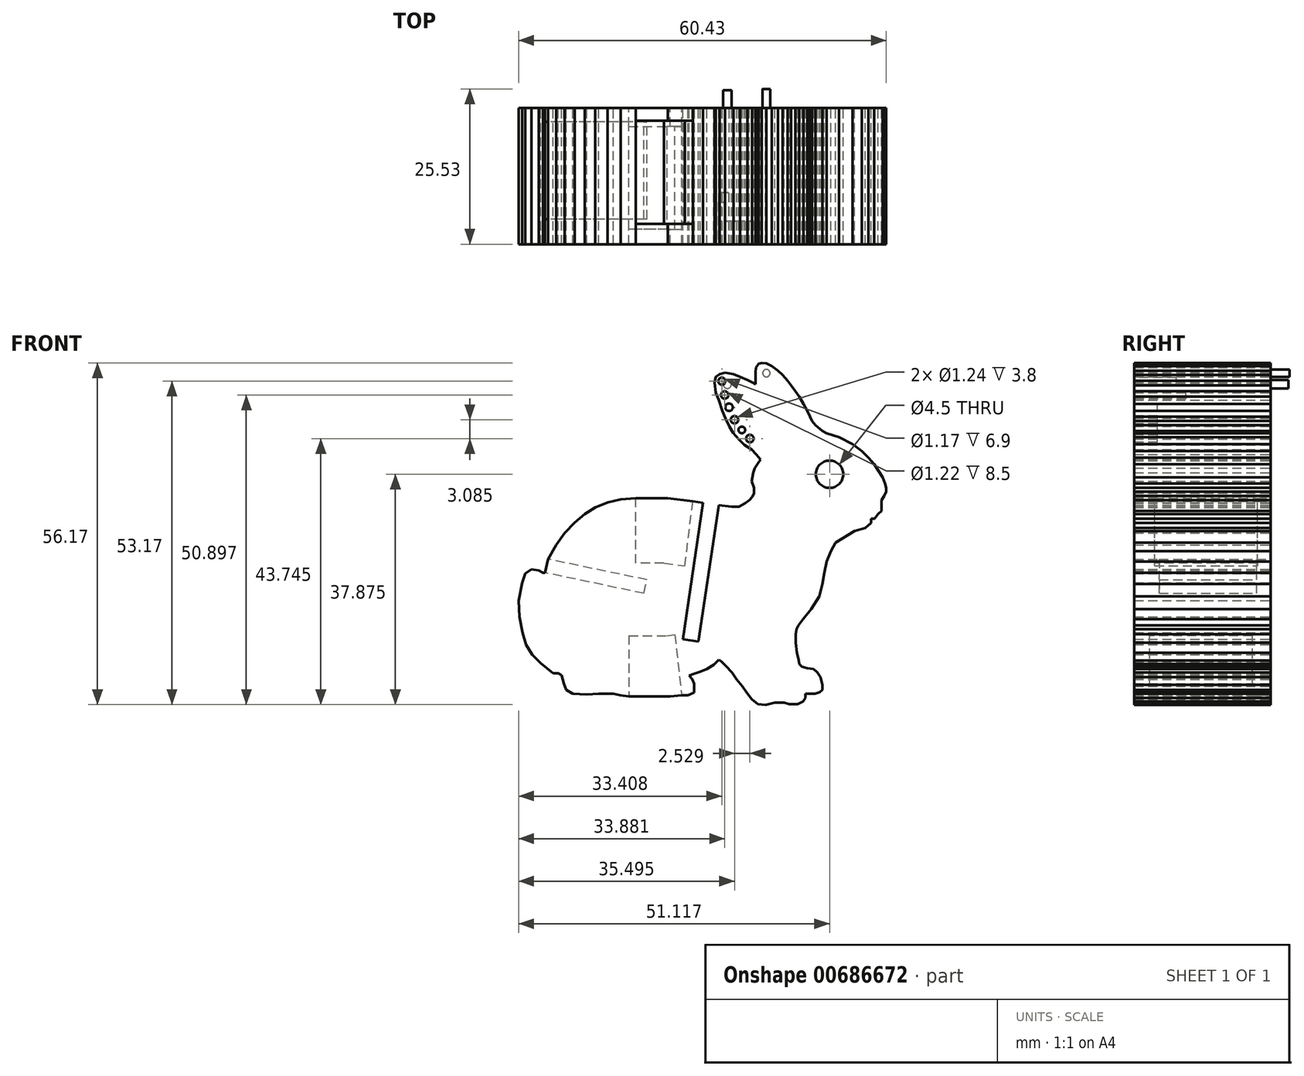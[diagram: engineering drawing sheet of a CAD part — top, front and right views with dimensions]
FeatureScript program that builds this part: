
annotation { "Feature Type Name" : "Feature", "Feature Type Description" : "" }
export const myFeature = defineFeature(function(context is Context, id is Id, definition is map)
    precondition{}
    {
        {
            var Q0;
            Q0=qCreatedBy(makeId("Front.planeOp"),FACE);
            var sketch = newSketch(context, id + "F0", { "sketchPlane" : qUnion([Q0])});
            skLineSegment(sketch, "E0", {"start": v(59.18, 31.9) * mm, "end": v(59.18, 31.2) * mm});
            skLineSegment(sketch, "E1", {"start": v(59.18, 31.2) * mm, "end": v(58.21, 30.37) * mm});
            skLineSegment(sketch, "E2", {"start": v(58.21, 30.37) * mm, "end": v(56.46, 29.85) * mm});
            skLineSegment(sketch, "E3", {"start": v(56.46, 29.85) * mm, "end": v(53.36, 27.96) * mm});
            skLineSegment(sketch, "E4", {"start": v(53.36, 27.96) * mm, "end": v(52.57, 26.52) * mm});
            skLineSegment(sketch, "E5", {"start": v(52.57, 26.52) * mm, "end": v(51.91, 24.8) * mm});
            skLineSegment(sketch, "E6", {"start": v(51.91, 24.8) * mm, "end": v(51.53, 22.99) * mm});
            skLineSegment(sketch, "E7", {"start": v(51.53, 22.99) * mm, "end": v(51.19, 21.11) * mm});
            skLineSegment(sketch, "E8", {"start": v(51.19, 21.11) * mm, "end": v(50.68, 19.1) * mm});
            skLineSegment(sketch, "E9", {"start": v(50.68, 19.1) * mm, "end": v(49.32, 17.01) * mm});
            skLineSegment(sketch, "E10", {"start": v(49.32, 17.01) * mm, "end": v(48.02, 15.39) * mm});
            skLineSegment(sketch, "E11", {"start": v(48.02, 15.39) * mm, "end": v(47.24, 14.33) * mm});
            skLineSegment(sketch, "E12", {"start": v(47.24, 14.33) * mm, "end": v(46.93, 13.71) * mm});
            skLineSegment(sketch, "E13", {"start": v(46.93, 13.71) * mm, "end": v(46.8, 12.88) * mm});
            skLineSegment(sketch, "E14", {"start": v(46.8, 12.88) * mm, "end": v(46.8, 11.49) * mm});
            skLineSegment(sketch, "E15", {"start": v(46.8, 11.49) * mm, "end": v(47.02, 9.82) * mm});
            skLineSegment(sketch, "E16", {"start": v(47.02, 9.82) * mm, "end": v(47.3, 8.54) * mm});
            skLineSegment(sketch, "E17", {"start": v(47.3, 8.54) * mm, "end": v(47.4, 8) * mm});
            skLineSegment(sketch, "E18", {"start": v(47.4, 8) * mm, "end": v(47.8, 7.53) * mm});
            skLineSegment(sketch, "E19", {"start": v(47.8, 7.53) * mm, "end": v(48.73, 7.33) * mm});
            skLineSegment(sketch, "E20", {"start": v(48.73, 7.33) * mm, "end": v(49.72, 7.17) * mm});
            skLineSegment(sketch, "E21", {"start": v(49.72, 7.17) * mm, "end": v(50.33, 6.61) * mm});
            skLineSegment(sketch, "E22", {"start": v(50.33, 6.61) * mm, "end": v(50.85, 5.82) * mm});
            skLineSegment(sketch, "E23", {"start": v(50.85, 5.82) * mm, "end": v(51.16, 4.55) * mm});
            skLineSegment(sketch, "E24", {"start": v(51.16, 4.55) * mm, "end": v(51.16, 3.77) * mm});
            skLineSegment(sketch, "E25", {"start": v(51.16, 3.77) * mm, "end": v(50.77, 3.37) * mm});
            skLineSegment(sketch, "E26", {"start": v(50.77, 3.37) * mm, "end": v(49.97, 3.1) * mm});
            skLineSegment(sketch, "E27", {"start": v(49.97, 3.1) * mm, "end": v(48.4, 3.1) * mm});
            skLineSegment(sketch, "E28", {"start": v(48.4, 3.1) * mm, "end": v(48.4, 2.43) * mm});
            skLineSegment(sketch, "E29", {"start": v(48.4, 2.43) * mm, "end": v(48.04, 1.82) * mm});
            skLineSegment(sketch, "E30", {"start": v(48.04, 1.82) * mm, "end": v(47.14, 1.41) * mm});
            skLineSegment(sketch, "E31", {"start": v(47.14, 1.41) * mm, "end": v(45.74, 1.41) * mm});
            skLineSegment(sketch, "E32", {"start": v(45.74, 1.41) * mm, "end": v(44.91, 1.62) * mm});
            skLineSegment(sketch, "E33", {"start": v(44.91, 1.62) * mm, "end": v(43.35, 1.62) * mm});
            skLineSegment(sketch, "E34", {"start": v(43.35, 1.62) * mm, "end": v(41.85, 1.3) * mm});
            skLineSegment(sketch, "E35", {"start": v(41.85, 1.3) * mm, "end": v(40.56, 1.41) * mm});
            skLineSegment(sketch, "E36", {"start": v(40.56, 1.41) * mm, "end": v(39.54, 2.2) * mm});
            skLineSegment(sketch, "E37", {"start": v(39.54, 2.2) * mm, "end": v(38.77, 3.29) * mm});
            skLineSegment(sketch, "E38", {"start": v(38.77, 3.29) * mm, "end": v(38.07, 4.3) * mm});
            skLineSegment(sketch, "E39", {"start": v(38.07, 4.3) * mm, "end": v(37.07, 5.46) * mm});
            skLineSegment(sketch, "E40", {"start": v(37.07, 5.46) * mm, "end": v(36.3, 6.57) * mm});
            skLineSegment(sketch, "E41", {"start": v(36.3, 6.57) * mm, "end": v(35.28, 7.7) * mm});
            skLineSegment(sketch, "E42", {"start": v(35.28, 7.7) * mm, "end": v(34.6, 8.39) * mm});
            skLineSegment(sketch, "E43", {"start": v(34.6, 8.39) * mm, "end": v(34.18, 8.68) * mm});
            skLineSegment(sketch, "E44", {"start": v(34.18, 8.68) * mm, "end": v(33.34, 7.84) * mm});
            skLineSegment(sketch, "E45", {"start": v(33.34, 7.84) * mm, "end": v(32.19, 7.18) * mm});
            skLineSegment(sketch, "E46", {"start": v(32.19, 7.18) * mm, "end": v(31.1, 6.72) * mm});
            skLineSegment(sketch, "E47", {"start": v(31.1, 6.72) * mm, "end": v(30.18, 6.39) * mm});
            skLineSegment(sketch, "E48", {"start": v(30.18, 6.39) * mm, "end": v(29.26, 6.12) * mm});
            skLineSegment(sketch, "E49", {"start": v(29.26, 6.12) * mm, "end": v(29.8, 5.51) * mm});
            skLineSegment(sketch, "E50", {"start": v(29.8, 5.51) * mm, "end": v(30.13, 4.73) * mm});
            skLineSegment(sketch, "E51", {"start": v(30.13, 4.73) * mm, "end": v(30.13, 4.07) * mm});
            skLineSegment(sketch, "E52", {"start": v(30.13, 4.07) * mm, "end": v(30.13, 3.51) * mm});
            skLineSegment(sketch, "E53", {"start": v(30.13, 3.51) * mm, "end": v(30.13, 3.29) * mm});
            skLineSegment(sketch, "E54", {"start": v(30.13, 3.29) * mm, "end": v(29.07, 2.88) * mm});
            skLineSegment(sketch, "E55", {"start": v(29.07, 2.88) * mm, "end": v(28.07, 2.88) * mm});
            skLineSegment(sketch, "E56", {"start": v(28.07, 2.88) * mm, "end": v(26.19, 2.66) * mm});
            skLineSegment(sketch, "E57", {"start": v(26.19, 2.66) * mm, "end": v(23.74, 2.66) * mm});
            skLineSegment(sketch, "E58", {"start": v(23.74, 2.66) * mm, "end": v(21.88, 2.66) * mm});
            skLineSegment(sketch, "E59", {"start": v(21.88, 2.66) * mm, "end": v(19.4, 2.66) * mm});
            skLineSegment(sketch, "E60", {"start": v(19.4, 2.66) * mm, "end": v(18, 2.88) * mm});
            skLineSegment(sketch, "E61", {"start": v(18, 2.88) * mm, "end": v(16.82, 3.14) * mm});
            skLineSegment(sketch, "E62", {"start": v(16.82, 3.14) * mm, "end": v(14.45, 3.14) * mm});
            skLineSegment(sketch, "E63", {"start": v(14.45, 3.14) * mm, "end": v(12.45, 3) * mm});
            skLineSegment(sketch, "E64", {"start": v(12.45, 3) * mm, "end": v(10.14, 3.13) * mm});
            skLineSegment(sketch, "E65", {"start": v(10.14, 3.13) * mm, "end": v(9.06, 3.73) * mm});
            skLineSegment(sketch, "E66", {"start": v(9.06, 3.73) * mm, "end": v(8.7, 4.73) * mm});
            skLineSegment(sketch, "E67", {"start": v(8.7, 4.73) * mm, "end": v(8.3, 6.14) * mm});
            skLineSegment(sketch, "E68", {"start": v(8.3, 6.14) * mm, "end": v(7.74, 6.47) * mm});
            skLineSegment(sketch, "E69", {"start": v(7.74, 6.47) * mm, "end": v(6.93, 6.47) * mm});
            skLineSegment(sketch, "E70", {"start": v(6.93, 6.47) * mm, "end": v(4.9, 8.14) * mm});
            skLineSegment(sketch, "E71", {"start": v(4.9, 8.14) * mm, "end": v(3.53, 9.54) * mm});
            skLineSegment(sketch, "E72", {"start": v(3.53, 9.54) * mm, "end": v(2.47, 11.15) * mm});
            skLineSegment(sketch, "E73", {"start": v(2.47, 11.15) * mm, "end": v(1.9, 13.14) * mm});
            skLineSegment(sketch, "E74", {"start": v(1.9, 13.14) * mm, "end": v(1.4, 15.75) * mm});
            skLineSegment(sketch, "E75", {"start": v(1.4, 15.75) * mm, "end": v(1.25, 18.43) * mm});
            skLineSegment(sketch, "E76", {"start": v(1.25, 18.43) * mm, "end": v(1.86, 21.3) * mm});
            skLineSegment(sketch, "E77", {"start": v(1.86, 21.3) * mm, "end": v(2.39, 22.87) * mm});
            skLineSegment(sketch, "E78", {"start": v(2.39, 22.87) * mm, "end": v(3.37, 23.56) * mm});
            skLineSegment(sketch, "E79", {"start": v(3.37, 23.56) * mm, "end": v(4.55, 23.4) * mm});
            skLineSegment(sketch, "E80", {"start": v(4.55, 23.4) * mm, "end": v(5.28, 22.99) * mm});
            skLineSegment(sketch, "E81", {"start": v(5.28, 22.99) * mm, "end": v(5.63, 22.99) * mm});
            skLineSegment(sketch, "E82", {"start": v(5.63, 22.99) * mm, "end": v(6.1, 25.22) * mm});
            skLineSegment(sketch, "E83", {"start": v(6.1, 25.22) * mm, "end": v(7.44, 27.53) * mm});
            skLineSegment(sketch, "E84", {"start": v(7.44, 27.53) * mm, "end": v(8.84, 29.53) * mm});
            skLineSegment(sketch, "E85", {"start": v(8.84, 29.53) * mm, "end": v(10.46, 31.27) * mm});
            skLineSegment(sketch, "E86", {"start": v(10.46, 31.27) * mm, "end": v(12.13, 32.66) * mm});
            skLineSegment(sketch, "E87", {"start": v(12.13, 32.66) * mm, "end": v(13.85, 33.74) * mm});
            skLineSegment(sketch, "E88", {"start": v(13.85, 33.74) * mm, "end": v(15.89, 34.56) * mm});
            skLineSegment(sketch, "E89", {"start": v(15.89, 34.56) * mm, "end": v(18.07, 35.02) * mm});
            skLineSegment(sketch, "E90", {"start": v(18.07, 35.02) * mm, "end": v(20.5, 35.25) * mm});
            skLineSegment(sketch, "E91", {"start": v(20.5, 35.25) * mm, "end": v(22.93, 35.25) * mm});
            skLineSegment(sketch, "E92", {"start": v(22.93, 35.25) * mm, "end": v(25.8, 35.25) * mm});
            skLineSegment(sketch, "E93", {"start": v(25.8, 35.25) * mm, "end": v(29.9, 34.74) * mm});
            skLineSegment(sketch, "E94", {"start": v(29.9, 34.74) * mm, "end": v(31.58, 34.5) * mm});
            skLineSegment(sketch, "E95", {"start": v(31.58, 34.5) * mm, "end": v(34.17, 34.11) * mm});
            skLineSegment(sketch, "E96", {"start": v(34.17, 34.11) * mm, "end": v(36.24, 33.84) * mm});
            skLineSegment(sketch, "E97", {"start": v(36.24, 33.84) * mm, "end": v(37.5, 33.84) * mm});
            skLineSegment(sketch, "E98", {"start": v(37.5, 33.84) * mm, "end": v(38.48, 34.41) * mm});
            skLineSegment(sketch, "E99", {"start": v(38.48, 34.41) * mm, "end": v(39.21, 34.95) * mm});
            skLineSegment(sketch, "E100", {"start": v(39.21, 34.95) * mm, "end": v(39.69, 35.51) * mm});
            skLineSegment(sketch, "E101", {"start": v(39.69, 35.51) * mm, "end": v(39.94, 36.1) * mm});
            skLineSegment(sketch, "E102", {"start": v(39.94, 36.1) * mm, "end": v(39.94, 36.93) * mm});
            skLineSegment(sketch, "E103", {"start": v(39.94, 36.93) * mm, "end": v(39.54, 38.02) * mm});
            skLineSegment(sketch, "E104", {"start": v(39.54, 38.02) * mm, "end": v(39.83, 39.44) * mm});
            skLineSegment(sketch, "E105", {"start": v(39.83, 39.44) * mm, "end": v(40.08, 40.2) * mm});
            skLineSegment(sketch, "E106", {"start": v(40.08, 40.2) * mm, "end": v(40.6, 40.94) * mm});
            skLineSegment(sketch, "E107", {"start": v(40.6, 40.94) * mm, "end": v(41, 41.61) * mm});
            skLineSegment(sketch, "E108", {"start": v(41, 41.61) * mm, "end": v(40.3, 42.4) * mm});
            skLineSegment(sketch, "E109", {"start": v(40.3, 42.4) * mm, "end": v(39.57, 43.22) * mm});
            skLineSegment(sketch, "E110", {"start": v(39.57, 43.22) * mm, "end": v(38.4, 44.03) * mm});
            skLineSegment(sketch, "E111", {"start": v(38.4, 44.03) * mm, "end": v(37.38, 44.92) * mm});
            skLineSegment(sketch, "E112", {"start": v(37.38, 44.92) * mm, "end": v(36.53, 45.97) * mm});
            skLineSegment(sketch, "E113", {"start": v(36.53, 45.97) * mm, "end": v(35.9, 47.05) * mm});
            skLineSegment(sketch, "E114", {"start": v(35.9, 47.05) * mm, "end": v(35.26, 48.39) * mm});
            skLineSegment(sketch, "E115", {"start": v(35.26, 48.39) * mm, "end": v(34.77, 49.59) * mm});
            skLineSegment(sketch, "E116", {"start": v(34.77, 49.59) * mm, "end": v(34.17, 51.34) * mm});
            skLineSegment(sketch, "E117", {"start": v(34.17, 51.34) * mm, "end": v(33.68, 52.6) * mm});
            skLineSegment(sketch, "E118", {"start": v(33.68, 52.6) * mm, "end": v(33.5, 54.23) * mm});
            skLineSegment(sketch, "E119", {"start": v(33.5, 54.23) * mm, "end": v(33.67, 55.17) * mm});
            skLineSegment(sketch, "E120", {"start": v(33.67, 55.17) * mm, "end": v(34.28, 55.63) * mm});
            skLineSegment(sketch, "E121", {"start": v(34.28, 55.63) * mm, "end": v(35.19, 55.89) * mm});
            skLineSegment(sketch, "E122", {"start": v(35.19, 55.89) * mm, "end": v(36.57, 55.6) * mm});
            skLineSegment(sketch, "E123", {"start": v(36.57, 55.6) * mm, "end": v(37.7, 55.18) * mm});
            skLineSegment(sketch, "E124", {"start": v(37.7, 55.18) * mm, "end": v(38.87, 54.67) * mm});
            skLineSegment(sketch, "E125", {"start": v(38.87, 54.67) * mm, "end": v(39.6, 54.27) * mm});
            skLineSegment(sketch, "E126", {"start": v(39.6, 54.27) * mm, "end": v(40.2, 53.98) * mm});
            skLineSegment(sketch, "E127", {"start": v(40.2, 53.98) * mm, "end": v(40.2, 55.95) * mm});
            skLineSegment(sketch, "E128", {"start": v(40.2, 55.95) * mm, "end": v(40.3, 56.68) * mm});
            skLineSegment(sketch, "E129", {"start": v(40.3, 56.68) * mm, "end": v(40.7, 57.32) * mm});
            skLineSegment(sketch, "E130", {"start": v(40.7, 57.32) * mm, "end": v(41.2, 57.47) * mm});
            skLineSegment(sketch, "E131", {"start": v(41.2, 57.47) * mm, "end": v(41.98, 57.38) * mm});
            skLineSegment(sketch, "E132", {"start": v(41.98, 57.38) * mm, "end": v(42.9, 56.96) * mm});
            skLineSegment(sketch, "E133", {"start": v(42.9, 56.96) * mm, "end": v(43.88, 56.18) * mm});
            skLineSegment(sketch, "E134", {"start": v(43.88, 56.18) * mm, "end": v(44.66, 55.47) * mm});
            skLineSegment(sketch, "E135", {"start": v(44.66, 55.47) * mm, "end": v(45.46, 54.57) * mm});
            skLineSegment(sketch, "E136", {"start": v(45.46, 54.57) * mm, "end": v(46.07, 53.8) * mm});
            skLineSegment(sketch, "E137", {"start": v(46.07, 53.8) * mm, "end": v(46.74, 52.83) * mm});
            skLineSegment(sketch, "E138", {"start": v(46.74, 52.83) * mm, "end": v(47.4, 51.92) * mm});
            skLineSegment(sketch, "E139", {"start": v(47.4, 51.92) * mm, "end": v(48.07, 50.76) * mm});
            skLineSegment(sketch, "E140", {"start": v(48.07, 50.76) * mm, "end": v(48.69, 49.58) * mm});
            skLineSegment(sketch, "E141", {"start": v(48.69, 49.58) * mm, "end": v(49.16, 48.64) * mm});
            skLineSegment(sketch, "E142", {"start": v(49.16, 48.64) * mm, "end": v(49.5, 47.92) * mm});
            skLineSegment(sketch, "E143", {"start": v(49.5, 47.92) * mm, "end": v(50.03, 47.25) * mm});
            skLineSegment(sketch, "E144", {"start": v(50.03, 47.25) * mm, "end": v(51.16, 46.28) * mm});
            skLineSegment(sketch, "E145", {"start": v(51.16, 46.28) * mm, "end": v(51.87, 45.89) * mm});
            skLineSegment(sketch, "E146", {"start": v(51.87, 45.89) * mm, "end": v(53.94, 45.3) * mm});
            skLineSegment(sketch, "E147", {"start": v(53.94, 45.3) * mm, "end": v(56.13, 44.1) * mm});
            skLineSegment(sketch, "E148", {"start": v(56.13, 44.1) * mm, "end": v(57.69, 42.96) * mm});
            skLineSegment(sketch, "E149", {"start": v(57.69, 42.96) * mm, "end": v(58.76, 41.92) * mm});
            skLineSegment(sketch, "E150", {"start": v(58.76, 41.92) * mm, "end": v(59.7, 40.84) * mm});
            skLineSegment(sketch, "E151", {"start": v(59.7, 40.84) * mm, "end": v(60.39, 39.73) * mm});
            skLineSegment(sketch, "E152", {"start": v(60.39, 39.73) * mm, "end": v(61.06, 38.64) * mm});
            skLineSegment(sketch, "E153", {"start": v(61.06, 38.64) * mm, "end": v(61.48, 37.65) * mm});
            skLineSegment(sketch, "E154", {"start": v(61.48, 37.65) * mm, "end": v(61.68, 36.96) * mm});
            skLineSegment(sketch, "E155", {"start": v(61.68, 36.96) * mm, "end": v(61.68, 36.3) * mm});
            skLineSegment(sketch, "E156", {"start": v(61.68, 36.3) * mm, "end": v(61.36, 35.64) * mm});
            skLineSegment(sketch, "E157", {"start": v(61.36, 35.64) * mm, "end": v(60.9, 34.95) * mm});
            skLineSegment(sketch, "E158", {"start": v(60.9, 34.95) * mm, "end": v(60.9, 33.94) * mm});
            skLineSegment(sketch, "E159", {"start": v(60.9, 33.94) * mm, "end": v(60.9, 33.16) * mm});
            skLineSegment(sketch, "E160", {"start": v(60.9, 33.16) * mm, "end": v(60.3, 32.6) * mm});
            skLineSegment(sketch, "E161", {"start": v(60.3, 32.6) * mm, "end": v(59.74, 31.88) * mm});
            skLineSegment(sketch, "E162", {"start": v(59.74, 31.88) * mm, "end": v(59.18, 31.9) * mm});
            skCircle(sketch, "E163", {"center": v(52.37, 39.17) * mm, "radius": 2.25 * mm});
            skSolve(sketch);
        }
        {
            var Q0;
            Q0=makeQuery(id+"F0.imprint","IMPRINT",FACE,{"disambiguationData":[TD([[makeQuery(id+"F0.imprint","IMPRINT",EDGE,{"derivedFrom":sQuery(id+"F0.wireOp",EDGE,"E0")}),-1.0]])]});
            extrude(context, id + "F1", {"entities" : qUnion([Q0]), "depth" : 3 * mm, "offsetDistance" : 25 * mm});
        }
        {
            var Q0;
            Q0=makeQuery(id+"F1.opExtrude","CAP_FACE",FACE,{"disambiguationData":[OSD([sQuery(id+"F0.wireOp",EDGE,"E0"),sQuery(id+"F0.wireOp",EDGE,"E1"),sQuery(id+"F0.wireOp",EDGE,"E2"),sQuery(id+"F0.wireOp",EDGE,"E3"),sQuery(id+"F0.wireOp",EDGE,"E4"),sQuery(id+"F0.wireOp",EDGE,"E5"),sQuery(id+"F0.wireOp",EDGE,"E6"),sQuery(id+"F0.wireOp",EDGE,"E7"),sQuery(id+"F0.wireOp",EDGE,"E8"),sQuery(id+"F0.wireOp",EDGE,"E9"),sQuery(id+"F0.wireOp",EDGE,"E10"),sQuery(id+"F0.wireOp",EDGE,"E11"),sQuery(id+"F0.wireOp",EDGE,"E12"),sQuery(id+"F0.wireOp",EDGE,"E13"),sQuery(id+"F0.wireOp",EDGE,"E14"),sQuery(id+"F0.wireOp",EDGE,"E15"),sQuery(id+"F0.wireOp",EDGE,"E16"),sQuery(id+"F0.wireOp",EDGE,"E17"),sQuery(id+"F0.wireOp",EDGE,"E18"),sQuery(id+"F0.wireOp",EDGE,"E19"),sQuery(id+"F0.wireOp",EDGE,"E20"),sQuery(id+"F0.wireOp",EDGE,"E21"),sQuery(id+"F0.wireOp",EDGE,"E22"),sQuery(id+"F0.wireOp",EDGE,"E23"),sQuery(id+"F0.wireOp",EDGE,"E24"),sQuery(id+"F0.wireOp",EDGE,"E25"),sQuery(id+"F0.wireOp",EDGE,"E26"),sQuery(id+"F0.wireOp",EDGE,"E27"),sQuery(id+"F0.wireOp",EDGE,"E28"),sQuery(id+"F0.wireOp",EDGE,"E29"),sQuery(id+"F0.wireOp",EDGE,"E30"),sQuery(id+"F0.wireOp",EDGE,"E31"),sQuery(id+"F0.wireOp",EDGE,"E32"),sQuery(id+"F0.wireOp",EDGE,"E33"),sQuery(id+"F0.wireOp",EDGE,"E34"),sQuery(id+"F0.wireOp",EDGE,"E35"),sQuery(id+"F0.wireOp",EDGE,"E36"),sQuery(id+"F0.wireOp",EDGE,"E37"),sQuery(id+"F0.wireOp",EDGE,"E38"),sQuery(id+"F0.wireOp",EDGE,"E39"),sQuery(id+"F0.wireOp",EDGE,"E40"),sQuery(id+"F0.wireOp",EDGE,"E41"),sQuery(id+"F0.wireOp",EDGE,"E42"),sQuery(id+"F0.wireOp",EDGE,"E43"),sQuery(id+"F0.wireOp",EDGE,"E44"),sQuery(id+"F0.wireOp",EDGE,"E45"),sQuery(id+"F0.wireOp",EDGE,"E46"),sQuery(id+"F0.wireOp",EDGE,"E47"),sQuery(id+"F0.wireOp",EDGE,"E48"),sQuery(id+"F0.wireOp",EDGE,"E49"),sQuery(id+"F0.wireOp",EDGE,"E50"),sQuery(id+"F0.wireOp",EDGE,"E51"),sQuery(id+"F0.wireOp",EDGE,"E52"),sQuery(id+"F0.wireOp",EDGE,"E53"),sQuery(id+"F0.wireOp",EDGE,"E54"),sQuery(id+"F0.wireOp",EDGE,"E55"),sQuery(id+"F0.wireOp",EDGE,"E56"),sQuery(id+"F0.wireOp",EDGE,"E57"),sQuery(id+"F0.wireOp",EDGE,"E58"),sQuery(id+"F0.wireOp",EDGE,"E59"),sQuery(id+"F0.wireOp",EDGE,"E60"),sQuery(id+"F0.wireOp",EDGE,"E61"),sQuery(id+"F0.wireOp",EDGE,"E62"),sQuery(id+"F0.wireOp",EDGE,"E63"),sQuery(id+"F0.wireOp",EDGE,"E64"),sQuery(id+"F0.wireOp",EDGE,"E65"),sQuery(id+"F0.wireOp",EDGE,"E66"),sQuery(id+"F0.wireOp",EDGE,"E67"),sQuery(id+"F0.wireOp",EDGE,"E68"),sQuery(id+"F0.wireOp",EDGE,"E69"),sQuery(id+"F0.wireOp",EDGE,"E70"),sQuery(id+"F0.wireOp",EDGE,"E71"),sQuery(id+"F0.wireOp",EDGE,"E72"),sQuery(id+"F0.wireOp",EDGE,"E73"),sQuery(id+"F0.wireOp",EDGE,"E74"),sQuery(id+"F0.wireOp",EDGE,"E75"),sQuery(id+"F0.wireOp",EDGE,"E76"),sQuery(id+"F0.wireOp",EDGE,"E77"),sQuery(id+"F0.wireOp",EDGE,"E78"),sQuery(id+"F0.wireOp",EDGE,"E79"),sQuery(id+"F0.wireOp",EDGE,"E80"),sQuery(id+"F0.wireOp",EDGE,"E81"),sQuery(id+"F0.wireOp",EDGE,"E82"),sQuery(id+"F0.wireOp",EDGE,"E83"),sQuery(id+"F0.wireOp",EDGE,"E84"),sQuery(id+"F0.wireOp",EDGE,"E85"),sQuery(id+"F0.wireOp",EDGE,"E86"),sQuery(id+"F0.wireOp",EDGE,"E87"),sQuery(id+"F0.wireOp",EDGE,"E88"),sQuery(id+"F0.wireOp",EDGE,"E89"),sQuery(id+"F0.wireOp",EDGE,"E90"),sQuery(id+"F0.wireOp",EDGE,"E91"),sQuery(id+"F0.wireOp",EDGE,"E92"),sQuery(id+"F0.wireOp",EDGE,"E93"),sQuery(id+"F0.wireOp",EDGE,"E94"),sQuery(id+"F0.wireOp",EDGE,"E95"),sQuery(id+"F0.wireOp",EDGE,"E96"),sQuery(id+"F0.wireOp",EDGE,"E97"),sQuery(id+"F0.wireOp",EDGE,"E98"),sQuery(id+"F0.wireOp",EDGE,"E99"),sQuery(id+"F0.wireOp",EDGE,"E100"),sQuery(id+"F0.wireOp",EDGE,"E101"),sQuery(id+"F0.wireOp",EDGE,"E102"),sQuery(id+"F0.wireOp",EDGE,"E103"),sQuery(id+"F0.wireOp",EDGE,"E104"),sQuery(id+"F0.wireOp",EDGE,"E105"),sQuery(id+"F0.wireOp",EDGE,"E106"),sQuery(id+"F0.wireOp",EDGE,"E107"),sQuery(id+"F0.wireOp",EDGE,"E108"),sQuery(id+"F0.wireOp",EDGE,"E109"),sQuery(id+"F0.wireOp",EDGE,"E110"),sQuery(id+"F0.wireOp",EDGE,"E111"),sQuery(id+"F0.wireOp",EDGE,"E112"),sQuery(id+"F0.wireOp",EDGE,"E113"),sQuery(id+"F0.wireOp",EDGE,"E114"),sQuery(id+"F0.wireOp",EDGE,"E115"),sQuery(id+"F0.wireOp",EDGE,"E116"),sQuery(id+"F0.wireOp",EDGE,"E117"),sQuery(id+"F0.wireOp",EDGE,"E118"),sQuery(id+"F0.wireOp",EDGE,"E119"),sQuery(id+"F0.wireOp",EDGE,"E120"),sQuery(id+"F0.wireOp",EDGE,"E121"),sQuery(id+"F0.wireOp",EDGE,"E122"),sQuery(id+"F0.wireOp",EDGE,"E123"),sQuery(id+"F0.wireOp",EDGE,"E124"),sQuery(id+"F0.wireOp",EDGE,"E125"),sQuery(id+"F0.wireOp",EDGE,"E126"),sQuery(id+"F0.wireOp",EDGE,"E127"),sQuery(id+"F0.wireOp",EDGE,"E128"),sQuery(id+"F0.wireOp",EDGE,"E129"),sQuery(id+"F0.wireOp",EDGE,"E130"),sQuery(id+"F0.wireOp",EDGE,"E131"),sQuery(id+"F0.wireOp",EDGE,"E132"),sQuery(id+"F0.wireOp",EDGE,"E133"),sQuery(id+"F0.wireOp",EDGE,"E134"),sQuery(id+"F0.wireOp",EDGE,"E135"),sQuery(id+"F0.wireOp",EDGE,"E136"),sQuery(id+"F0.wireOp",EDGE,"E137"),sQuery(id+"F0.wireOp",EDGE,"E138"),sQuery(id+"F0.wireOp",EDGE,"E139"),sQuery(id+"F0.wireOp",EDGE,"E140"),sQuery(id+"F0.wireOp",EDGE,"E141"),sQuery(id+"F0.wireOp",EDGE,"E142"),sQuery(id+"F0.wireOp",EDGE,"E143"),sQuery(id+"F0.wireOp",EDGE,"E144"),sQuery(id+"F0.wireOp",EDGE,"E145"),sQuery(id+"F0.wireOp",EDGE,"E146"),sQuery(id+"F0.wireOp",EDGE,"E147"),sQuery(id+"F0.wireOp",EDGE,"E148"),sQuery(id+"F0.wireOp",EDGE,"E149"),sQuery(id+"F0.wireOp",EDGE,"E150"),sQuery(id+"F0.wireOp",EDGE,"E151"),sQuery(id+"F0.wireOp",EDGE,"E152"),sQuery(id+"F0.wireOp",EDGE,"E153"),sQuery(id+"F0.wireOp",EDGE,"E154"),sQuery(id+"F0.wireOp",EDGE,"E155"),sQuery(id+"F0.wireOp",EDGE,"E156"),sQuery(id+"F0.wireOp",EDGE,"E157"),sQuery(id+"F0.wireOp",EDGE,"E158"),sQuery(id+"F0.wireOp",EDGE,"E159"),sQuery(id+"F0.wireOp",EDGE,"E160"),sQuery(id+"F0.wireOp",EDGE,"E161"),sQuery(id+"F0.wireOp",EDGE,"E162"),sQuery(id+"F0.wireOp",EDGE,"E163")])],"isStart":false});
            extrude(context, id + "F2", {"entities" : qUnion([Q0]), "operationType" : NewBodyOperationType.ADD, "depth" : 19.4 * mm, "offsetDistance" : 25 * mm});
        }
        {
            var Q0;
            {var subQ0=sQuery(id+"F0.wireOp",EDGE,"E95");Q0=makeQuery(id+"F2.boolean.opBoolean","MERGE",FACE,{"derivedFrom":[makeQuery(id+"F1.opExtrude","SWEPT_FACE",FACE,{"disambiguationData":[OSD([subQ0])]}),makeQuery(id+"F2.opExtrude","SWEPT_FACE",FACE,{"disambiguationData":[OSD([subQ0])]})]});}
            extrude(context, id + "F3", {"entities" : qUnion([Q0]), "operationType" : NewBodyOperationType.REMOVE, "oppositeDirection" : true, "depth" : 15.7 * mm, "offsetDistance" : 25 * mm});
        }
        {
            var Q0;
            Q0=makeQuery(id+"F3.boolean.opBoolean","COPY",FACE,{"derivedFrom":makeQuery(id+"F3.opExtrude","CAP_FACE",FACE,{"disambiguationData":[OSD([sQuery(id+"F0.wireOp",EDGE,"E95")])],"isStart":false})});
            extrude(context, id + "F4", {"entities" : qUnion([Q0]), "operationType" : NewBodyOperationType.REMOVE, "oppositeDirection" : true, "depth" : 7 * mm, "offsetDistance" : 25 * mm});
        }
        {
            var Q0;
            {var subQ0=sQuery(id+"F0.wireOp",EDGE,"E93");Q0=makeQuery(id+"F2.boolean.opBoolean","MERGE",FACE,{"derivedFrom":[makeQuery(id+"F1.opExtrude","SWEPT_FACE",FACE,{"disambiguationData":[OSD([subQ0])]}),makeQuery(id+"F2.opExtrude","SWEPT_FACE",FACE,{"disambiguationData":[OSD([subQ0])]})]});}
            var sketch = newSketch(context, id + "F5", { "sketchPlane" : qUnion([Q0])});
            skLineSegment(sketch, "E164", {"start": v(21.27, -2.12) * mm, "end": v(25.4, -2.12) * mm});
            skLineSegment(sketch, "E165", {"start": v(25.4, -2.12) * mm, "end": v(25.4, -19.03) * mm});
            skLineSegment(sketch, "E166", {"start": v(25.4, -19.03) * mm, "end": v(21.27, -19.03) * mm});
            skLineSegment(sketch, "E167", {"start": v(21.27, -19.03) * mm, "end": v(21.27, -2.12) * mm});
            skSolve(sketch);
        }
        {
            var Q0;
            Q0 = qSketchRegion(id + "F5", true);
            extrude(context, id + "F6", {"entities" : qUnion([Q0]), "operationType" : NewBodyOperationType.REMOVE, "oppositeDirection" : true, "depth" : 10.7 * mm, "offsetDistance" : 25 * mm});
        }
        {
            var Q0;
            {var subQ0=sQuery(id+"F0.wireOp",EDGE,"E92");var subQ1=sQuery(id+"F0.wireOp",EDGE,"E91");Q0=makeQuery(id+"F2.boolean.opBoolean","MERGE",FACE,{"derivedFrom":[makeQuery(id+"F1.opExtrude","SWEPT_FACE",FACE,{"disambiguationData":[OSD([subQ1,subQ0])]}),makeQuery(id+"F2.opExtrude","SWEPT_FACE",FACE,{"disambiguationData":[OSD([subQ1,subQ0])]})]});}
            var sketch = newSketch(context, id + "F7", { "sketchPlane" : qUnion([Q0])});
            skLineSegment(sketch, "E168", {"start": v(25.8, -2.12) * mm, "end": v(20.5, -2.12) * mm});
            skLineSegment(sketch, "E169", {"start": v(20.5, -2.12) * mm, "end": v(20.5, -19.03) * mm});
            skLineSegment(sketch, "E170", {"start": v(20.5, -19.03) * mm, "end": v(25.8, -19.03) * mm});
            skSolve(sketch);
        }
        {
            var Q0;
            Q0 = qSketchRegion(id + "F7", true);
            var Q1;
            Q1=makeQuery(id+"F7.imprint","IMPRINT",FACE,{"disambiguationData":[TD([[makeQuery(id+"F7.imprint","IMPRINT",EDGE,{"derivedFrom":sQuery(id+"F7.wireOp",EDGE,"E168")}),1.0]])]});
            extrude(context, id + "F8", {"entities" : qUnion([Q0, Q1]), "operationType" : NewBodyOperationType.REMOVE, "oppositeDirection" : true, "depth" : 10.7 * mm, "offsetDistance" : 25 * mm});
        }
        {
            var Q0;
            {var subQ0=sQuery(id+"F0.wireOp",EDGE,"E82");Q0=makeQuery(id+"F2.boolean.opBoolean","MERGE",FACE,{"derivedFrom":[makeQuery(id+"F1.opExtrude","SWEPT_FACE",FACE,{"disambiguationData":[OSD([subQ0])]}),makeQuery(id+"F2.opExtrude","SWEPT_FACE",FACE,{"disambiguationData":[OSD([subQ0])]})]});}
            var sketch = newSketch(context, id + "F9", { "sketchPlane" : qUnion([Q0])});
            skLineSegment(sketch, "E171", {"start": v(2.25, 23.65) * mm, "end": v(2.25, 25.93) * mm});
            skLineSegment(sketch, "E172", {"start": v(2.25, 25.93) * mm, "end": v(18.29, 25.93) * mm});
            skLineSegment(sketch, "E173", {"start": v(18.29, 25.93) * mm, "end": v(18.29, 23.65) * mm});
            skLineSegment(sketch, "E174", {"start": v(18.29, 23.65) * mm, "end": v(2.25, 23.65) * mm});
            skSolve(sketch);
        }
        {
            var Q0;
            Q0 = qSketchRegion(id + "F9", true);
            extrude(context, id + "F10", {"entities" : qUnion([Q0]), "operationType" : NewBodyOperationType.REMOVE, "oppositeDirection" : true, "depth" : 16.6 * mm, "offsetDistance" : 25 * mm});
        }
        {
            var Q0;
            {var subQ0=sQuery(id+"F0.wireOp",EDGE,"E59");var subQ1=sQuery(id+"F0.wireOp",EDGE,"E58");var subQ2=sQuery(id+"F0.wireOp",EDGE,"E57");Q0=makeQuery(id+"F2.boolean.opBoolean","MERGE",FACE,{"derivedFrom":[makeQuery(id+"F1.opExtrude","SWEPT_FACE",FACE,{"disambiguationData":[OSD([subQ2,subQ1,subQ0])]}),makeQuery(id+"F2.opExtrude","SWEPT_FACE",FACE,{"disambiguationData":[OSD([subQ2,subQ1,subQ0])]})]});}
            var sketch = newSketch(context, id + "F11", { "sketchPlane" : qUnion([Q0])});
            skLineSegment(sketch, "E175", {"start": v(26.19, 19.91) * mm, "end": v(19.4, 19.91) * mm});
            skLineSegment(sketch, "E176", {"start": v(19.4, 19.91) * mm, "end": v(19.4, 3.02) * mm});
            skLineSegment(sketch, "E177", {"start": v(19.4, 3.02) * mm, "end": v(26.19, 3.02) * mm});
            skLineSegment(sketch, "E178", {"start": v(26.19, 3.02) * mm, "end": v(26.19, 19.91) * mm});
            skSolve(sketch);
        }
        {
            var Q0;
            Q0 = qSketchRegion(id + "F11", true);
            extrude(context, id + "F12", {"entities" : qUnion([Q0]), "operationType" : NewBodyOperationType.REMOVE, "oppositeDirection" : true, "depth" : 10 * mm, "offsetDistance" : 25 * mm});
        }
        {
            var Q0;
            {var subQ0=sQuery(id+"F0.wireOp",EDGE,"E56");Q0=makeQuery(id+"F2.boolean.opBoolean","MERGE",FACE,{"derivedFrom":[makeQuery(id+"F1.opExtrude","SWEPT_FACE",FACE,{"disambiguationData":[OSD([subQ0])]}),makeQuery(id+"F2.opExtrude","SWEPT_FACE",FACE,{"disambiguationData":[OSD([subQ0])]})]});}
            var sketch = newSketch(context, id + "F13", { "sketchPlane" : qUnion([Q0])});
            skLineSegment(sketch, "E179", {"start": v(26.32, 19.91) * mm, "end": v(28.21, 19.91) * mm});
            skLineSegment(sketch, "E180", {"start": v(28.21, 19.91) * mm, "end": v(28.21, 3.02) * mm});
            skLineSegment(sketch, "E181", {"start": v(28.21, 3.02) * mm, "end": v(26.32, 3.02) * mm});
            skSolve(sketch);
        }
        {
            var Q0;
            Q0 = qSketchRegion(id + "F13", true);
            var Q1;
            Q1=makeQuery(id+"F13.imprint","IMPRINT",FACE,{"disambiguationData":[TD([[makeQuery(id+"F13.imprint","IMPRINT",EDGE,{"derivedFrom":sQuery(id+"F13.wireOp",EDGE,"E179")}),-1.0]])]});
            extrude(context, id + "F14", {"entities" : qUnion([Q0, Q1]), "operationType" : NewBodyOperationType.REMOVE, "oppositeDirection" : true, "depth" : 10 * mm, "offsetDistance" : 25 * mm});
        }
        {
            var Q0;
            Q0=makeQuery(id+"F2.opExtrude","CAP_FACE",FACE,{"disambiguationData":[OSD([sQuery(id+"F0.wireOp",EDGE,"E0"),sQuery(id+"F0.wireOp",EDGE,"E1"),sQuery(id+"F0.wireOp",EDGE,"E2"),sQuery(id+"F0.wireOp",EDGE,"E3"),sQuery(id+"F0.wireOp",EDGE,"E4"),sQuery(id+"F0.wireOp",EDGE,"E5"),sQuery(id+"F0.wireOp",EDGE,"E6"),sQuery(id+"F0.wireOp",EDGE,"E7"),sQuery(id+"F0.wireOp",EDGE,"E8"),sQuery(id+"F0.wireOp",EDGE,"E9"),sQuery(id+"F0.wireOp",EDGE,"E10"),sQuery(id+"F0.wireOp",EDGE,"E11"),sQuery(id+"F0.wireOp",EDGE,"E12"),sQuery(id+"F0.wireOp",EDGE,"E13"),sQuery(id+"F0.wireOp",EDGE,"E14"),sQuery(id+"F0.wireOp",EDGE,"E15"),sQuery(id+"F0.wireOp",EDGE,"E16"),sQuery(id+"F0.wireOp",EDGE,"E17"),sQuery(id+"F0.wireOp",EDGE,"E18"),sQuery(id+"F0.wireOp",EDGE,"E19"),sQuery(id+"F0.wireOp",EDGE,"E20"),sQuery(id+"F0.wireOp",EDGE,"E21"),sQuery(id+"F0.wireOp",EDGE,"E22"),sQuery(id+"F0.wireOp",EDGE,"E23"),sQuery(id+"F0.wireOp",EDGE,"E24"),sQuery(id+"F0.wireOp",EDGE,"E25"),sQuery(id+"F0.wireOp",EDGE,"E26"),sQuery(id+"F0.wireOp",EDGE,"E27"),sQuery(id+"F0.wireOp",EDGE,"E28"),sQuery(id+"F0.wireOp",EDGE,"E29"),sQuery(id+"F0.wireOp",EDGE,"E30"),sQuery(id+"F0.wireOp",EDGE,"E31"),sQuery(id+"F0.wireOp",EDGE,"E32"),sQuery(id+"F0.wireOp",EDGE,"E33"),sQuery(id+"F0.wireOp",EDGE,"E34"),sQuery(id+"F0.wireOp",EDGE,"E35"),sQuery(id+"F0.wireOp",EDGE,"E36"),sQuery(id+"F0.wireOp",EDGE,"E37"),sQuery(id+"F0.wireOp",EDGE,"E38"),sQuery(id+"F0.wireOp",EDGE,"E39"),sQuery(id+"F0.wireOp",EDGE,"E40"),sQuery(id+"F0.wireOp",EDGE,"E41"),sQuery(id+"F0.wireOp",EDGE,"E42"),sQuery(id+"F0.wireOp",EDGE,"E43"),sQuery(id+"F0.wireOp",EDGE,"E44"),sQuery(id+"F0.wireOp",EDGE,"E45"),sQuery(id+"F0.wireOp",EDGE,"E46"),sQuery(id+"F0.wireOp",EDGE,"E47"),sQuery(id+"F0.wireOp",EDGE,"E48"),sQuery(id+"F0.wireOp",EDGE,"E49"),sQuery(id+"F0.wireOp",EDGE,"E50"),sQuery(id+"F0.wireOp",EDGE,"E51"),sQuery(id+"F0.wireOp",EDGE,"E52"),sQuery(id+"F0.wireOp",EDGE,"E53"),sQuery(id+"F0.wireOp",EDGE,"E54"),sQuery(id+"F0.wireOp",EDGE,"E55"),sQuery(id+"F0.wireOp",EDGE,"E56"),sQuery(id+"F0.wireOp",EDGE,"E57"),sQuery(id+"F0.wireOp",EDGE,"E58"),sQuery(id+"F0.wireOp",EDGE,"E59"),sQuery(id+"F0.wireOp",EDGE,"E60"),sQuery(id+"F0.wireOp",EDGE,"E61"),sQuery(id+"F0.wireOp",EDGE,"E62"),sQuery(id+"F0.wireOp",EDGE,"E63"),sQuery(id+"F0.wireOp",EDGE,"E64"),sQuery(id+"F0.wireOp",EDGE,"E65"),sQuery(id+"F0.wireOp",EDGE,"E66"),sQuery(id+"F0.wireOp",EDGE,"E67"),sQuery(id+"F0.wireOp",EDGE,"E68"),sQuery(id+"F0.wireOp",EDGE,"E69"),sQuery(id+"F0.wireOp",EDGE,"E70"),sQuery(id+"F0.wireOp",EDGE,"E71"),sQuery(id+"F0.wireOp",EDGE,"E72"),sQuery(id+"F0.wireOp",EDGE,"E73"),sQuery(id+"F0.wireOp",EDGE,"E74"),sQuery(id+"F0.wireOp",EDGE,"E75"),sQuery(id+"F0.wireOp",EDGE,"E76"),sQuery(id+"F0.wireOp",EDGE,"E77"),sQuery(id+"F0.wireOp",EDGE,"E78"),sQuery(id+"F0.wireOp",EDGE,"E79"),sQuery(id+"F0.wireOp",EDGE,"E80"),sQuery(id+"F0.wireOp",EDGE,"E81"),sQuery(id+"F0.wireOp",EDGE,"E82"),sQuery(id+"F0.wireOp",EDGE,"E83"),sQuery(id+"F0.wireOp",EDGE,"E84"),sQuery(id+"F0.wireOp",EDGE,"E85"),sQuery(id+"F0.wireOp",EDGE,"E86"),sQuery(id+"F0.wireOp",EDGE,"E87"),sQuery(id+"F0.wireOp",EDGE,"E88"),sQuery(id+"F0.wireOp",EDGE,"E89"),sQuery(id+"F0.wireOp",EDGE,"E90"),sQuery(id+"F0.wireOp",EDGE,"E91"),sQuery(id+"F0.wireOp",EDGE,"E92"),sQuery(id+"F0.wireOp",EDGE,"E93"),sQuery(id+"F0.wireOp",EDGE,"E94"),sQuery(id+"F0.wireOp",EDGE,"E95"),sQuery(id+"F0.wireOp",EDGE,"E96"),sQuery(id+"F0.wireOp",EDGE,"E97"),sQuery(id+"F0.wireOp",EDGE,"E98"),sQuery(id+"F0.wireOp",EDGE,"E99"),sQuery(id+"F0.wireOp",EDGE,"E100"),sQuery(id+"F0.wireOp",EDGE,"E101"),sQuery(id+"F0.wireOp",EDGE,"E102"),sQuery(id+"F0.wireOp",EDGE,"E103"),sQuery(id+"F0.wireOp",EDGE,"E104"),sQuery(id+"F0.wireOp",EDGE,"E105"),sQuery(id+"F0.wireOp",EDGE,"E106"),sQuery(id+"F0.wireOp",EDGE,"E107"),sQuery(id+"F0.wireOp",EDGE,"E108"),sQuery(id+"F0.wireOp",EDGE,"E109"),sQuery(id+"F0.wireOp",EDGE,"E110"),sQuery(id+"F0.wireOp",EDGE,"E111"),sQuery(id+"F0.wireOp",EDGE,"E112"),sQuery(id+"F0.wireOp",EDGE,"E113"),sQuery(id+"F0.wireOp",EDGE,"E114"),sQuery(id+"F0.wireOp",EDGE,"E115"),sQuery(id+"F0.wireOp",EDGE,"E116"),sQuery(id+"F0.wireOp",EDGE,"E117"),sQuery(id+"F0.wireOp",EDGE,"E118"),sQuery(id+"F0.wireOp",EDGE,"E119"),sQuery(id+"F0.wireOp",EDGE,"E120"),sQuery(id+"F0.wireOp",EDGE,"E121"),sQuery(id+"F0.wireOp",EDGE,"E122"),sQuery(id+"F0.wireOp",EDGE,"E123"),sQuery(id+"F0.wireOp",EDGE,"E124"),sQuery(id+"F0.wireOp",EDGE,"E125"),sQuery(id+"F0.wireOp",EDGE,"E126"),sQuery(id+"F0.wireOp",EDGE,"E127"),sQuery(id+"F0.wireOp",EDGE,"E128"),sQuery(id+"F0.wireOp",EDGE,"E129"),sQuery(id+"F0.wireOp",EDGE,"E130"),sQuery(id+"F0.wireOp",EDGE,"E131"),sQuery(id+"F0.wireOp",EDGE,"E132"),sQuery(id+"F0.wireOp",EDGE,"E133"),sQuery(id+"F0.wireOp",EDGE,"E134"),sQuery(id+"F0.wireOp",EDGE,"E135"),sQuery(id+"F0.wireOp",EDGE,"E136"),sQuery(id+"F0.wireOp",EDGE,"E137"),sQuery(id+"F0.wireOp",EDGE,"E138"),sQuery(id+"F0.wireOp",EDGE,"E139"),sQuery(id+"F0.wireOp",EDGE,"E140"),sQuery(id+"F0.wireOp",EDGE,"E141"),sQuery(id+"F0.wireOp",EDGE,"E142"),sQuery(id+"F0.wireOp",EDGE,"E143"),sQuery(id+"F0.wireOp",EDGE,"E144"),sQuery(id+"F0.wireOp",EDGE,"E145"),sQuery(id+"F0.wireOp",EDGE,"E146"),sQuery(id+"F0.wireOp",EDGE,"E147"),sQuery(id+"F0.wireOp",EDGE,"E148"),sQuery(id+"F0.wireOp",EDGE,"E149"),sQuery(id+"F0.wireOp",EDGE,"E150"),sQuery(id+"F0.wireOp",EDGE,"E151"),sQuery(id+"F0.wireOp",EDGE,"E152"),sQuery(id+"F0.wireOp",EDGE,"E153"),sQuery(id+"F0.wireOp",EDGE,"E154"),sQuery(id+"F0.wireOp",EDGE,"E155"),sQuery(id+"F0.wireOp",EDGE,"E156"),sQuery(id+"F0.wireOp",EDGE,"E157"),sQuery(id+"F0.wireOp",EDGE,"E158"),sQuery(id+"F0.wireOp",EDGE,"E159"),sQuery(id+"F0.wireOp",EDGE,"E160"),sQuery(id+"F0.wireOp",EDGE,"E161"),sQuery(id+"F0.wireOp",EDGE,"E162"),sQuery(id+"F0.wireOp",EDGE,"E163")])],"isStart":false});
            var sketch = newSketch(context, id + "F15", { "sketchPlane" : qUnion([Q0])});
            skCircle(sketch, "E182", {"center": v(34.66, 54.47) * mm, "radius": 0.59 * mm});
            skSolve(sketch);
        }
        {
            var Q0;
            Q0 = qSketchRegion(id + "F15", true);
            extrude(context, id + "F16", {"entities" : qUnion([Q0]), "operationType" : NewBodyOperationType.REMOVE, "oppositeDirection" : true, "depth" : 6.9 * mm, "offsetDistance" : 25 * mm});
        }
        {
            var Q0;
            Q0=makeQuery(id+"F2.opExtrude","CAP_FACE",FACE,{"disambiguationData":[OSD([sQuery(id+"F0.wireOp",EDGE,"E0"),sQuery(id+"F0.wireOp",EDGE,"E1"),sQuery(id+"F0.wireOp",EDGE,"E2"),sQuery(id+"F0.wireOp",EDGE,"E3"),sQuery(id+"F0.wireOp",EDGE,"E4"),sQuery(id+"F0.wireOp",EDGE,"E5"),sQuery(id+"F0.wireOp",EDGE,"E6"),sQuery(id+"F0.wireOp",EDGE,"E7"),sQuery(id+"F0.wireOp",EDGE,"E8"),sQuery(id+"F0.wireOp",EDGE,"E9"),sQuery(id+"F0.wireOp",EDGE,"E10"),sQuery(id+"F0.wireOp",EDGE,"E11"),sQuery(id+"F0.wireOp",EDGE,"E12"),sQuery(id+"F0.wireOp",EDGE,"E13"),sQuery(id+"F0.wireOp",EDGE,"E14"),sQuery(id+"F0.wireOp",EDGE,"E15"),sQuery(id+"F0.wireOp",EDGE,"E16"),sQuery(id+"F0.wireOp",EDGE,"E17"),sQuery(id+"F0.wireOp",EDGE,"E18"),sQuery(id+"F0.wireOp",EDGE,"E19"),sQuery(id+"F0.wireOp",EDGE,"E20"),sQuery(id+"F0.wireOp",EDGE,"E21"),sQuery(id+"F0.wireOp",EDGE,"E22"),sQuery(id+"F0.wireOp",EDGE,"E23"),sQuery(id+"F0.wireOp",EDGE,"E24"),sQuery(id+"F0.wireOp",EDGE,"E25"),sQuery(id+"F0.wireOp",EDGE,"E26"),sQuery(id+"F0.wireOp",EDGE,"E27"),sQuery(id+"F0.wireOp",EDGE,"E28"),sQuery(id+"F0.wireOp",EDGE,"E29"),sQuery(id+"F0.wireOp",EDGE,"E30"),sQuery(id+"F0.wireOp",EDGE,"E31"),sQuery(id+"F0.wireOp",EDGE,"E32"),sQuery(id+"F0.wireOp",EDGE,"E33"),sQuery(id+"F0.wireOp",EDGE,"E34"),sQuery(id+"F0.wireOp",EDGE,"E35"),sQuery(id+"F0.wireOp",EDGE,"E36"),sQuery(id+"F0.wireOp",EDGE,"E37"),sQuery(id+"F0.wireOp",EDGE,"E38"),sQuery(id+"F0.wireOp",EDGE,"E39"),sQuery(id+"F0.wireOp",EDGE,"E40"),sQuery(id+"F0.wireOp",EDGE,"E41"),sQuery(id+"F0.wireOp",EDGE,"E42"),sQuery(id+"F0.wireOp",EDGE,"E43"),sQuery(id+"F0.wireOp",EDGE,"E44"),sQuery(id+"F0.wireOp",EDGE,"E45"),sQuery(id+"F0.wireOp",EDGE,"E46"),sQuery(id+"F0.wireOp",EDGE,"E47"),sQuery(id+"F0.wireOp",EDGE,"E48"),sQuery(id+"F0.wireOp",EDGE,"E49"),sQuery(id+"F0.wireOp",EDGE,"E50"),sQuery(id+"F0.wireOp",EDGE,"E51"),sQuery(id+"F0.wireOp",EDGE,"E52"),sQuery(id+"F0.wireOp",EDGE,"E53"),sQuery(id+"F0.wireOp",EDGE,"E54"),sQuery(id+"F0.wireOp",EDGE,"E55"),sQuery(id+"F0.wireOp",EDGE,"E56"),sQuery(id+"F0.wireOp",EDGE,"E57"),sQuery(id+"F0.wireOp",EDGE,"E58"),sQuery(id+"F0.wireOp",EDGE,"E59"),sQuery(id+"F0.wireOp",EDGE,"E60"),sQuery(id+"F0.wireOp",EDGE,"E61"),sQuery(id+"F0.wireOp",EDGE,"E62"),sQuery(id+"F0.wireOp",EDGE,"E63"),sQuery(id+"F0.wireOp",EDGE,"E64"),sQuery(id+"F0.wireOp",EDGE,"E65"),sQuery(id+"F0.wireOp",EDGE,"E66"),sQuery(id+"F0.wireOp",EDGE,"E67"),sQuery(id+"F0.wireOp",EDGE,"E68"),sQuery(id+"F0.wireOp",EDGE,"E69"),sQuery(id+"F0.wireOp",EDGE,"E70"),sQuery(id+"F0.wireOp",EDGE,"E71"),sQuery(id+"F0.wireOp",EDGE,"E72"),sQuery(id+"F0.wireOp",EDGE,"E73"),sQuery(id+"F0.wireOp",EDGE,"E74"),sQuery(id+"F0.wireOp",EDGE,"E75"),sQuery(id+"F0.wireOp",EDGE,"E76"),sQuery(id+"F0.wireOp",EDGE,"E77"),sQuery(id+"F0.wireOp",EDGE,"E78"),sQuery(id+"F0.wireOp",EDGE,"E79"),sQuery(id+"F0.wireOp",EDGE,"E80"),sQuery(id+"F0.wireOp",EDGE,"E81"),sQuery(id+"F0.wireOp",EDGE,"E82"),sQuery(id+"F0.wireOp",EDGE,"E83"),sQuery(id+"F0.wireOp",EDGE,"E84"),sQuery(id+"F0.wireOp",EDGE,"E85"),sQuery(id+"F0.wireOp",EDGE,"E86"),sQuery(id+"F0.wireOp",EDGE,"E87"),sQuery(id+"F0.wireOp",EDGE,"E88"),sQuery(id+"F0.wireOp",EDGE,"E89"),sQuery(id+"F0.wireOp",EDGE,"E90"),sQuery(id+"F0.wireOp",EDGE,"E91"),sQuery(id+"F0.wireOp",EDGE,"E92"),sQuery(id+"F0.wireOp",EDGE,"E93"),sQuery(id+"F0.wireOp",EDGE,"E94"),sQuery(id+"F0.wireOp",EDGE,"E95"),sQuery(id+"F0.wireOp",EDGE,"E96"),sQuery(id+"F0.wireOp",EDGE,"E97"),sQuery(id+"F0.wireOp",EDGE,"E98"),sQuery(id+"F0.wireOp",EDGE,"E99"),sQuery(id+"F0.wireOp",EDGE,"E100"),sQuery(id+"F0.wireOp",EDGE,"E101"),sQuery(id+"F0.wireOp",EDGE,"E102"),sQuery(id+"F0.wireOp",EDGE,"E103"),sQuery(id+"F0.wireOp",EDGE,"E104"),sQuery(id+"F0.wireOp",EDGE,"E105"),sQuery(id+"F0.wireOp",EDGE,"E106"),sQuery(id+"F0.wireOp",EDGE,"E107"),sQuery(id+"F0.wireOp",EDGE,"E108"),sQuery(id+"F0.wireOp",EDGE,"E109"),sQuery(id+"F0.wireOp",EDGE,"E110"),sQuery(id+"F0.wireOp",EDGE,"E111"),sQuery(id+"F0.wireOp",EDGE,"E112"),sQuery(id+"F0.wireOp",EDGE,"E113"),sQuery(id+"F0.wireOp",EDGE,"E114"),sQuery(id+"F0.wireOp",EDGE,"E115"),sQuery(id+"F0.wireOp",EDGE,"E116"),sQuery(id+"F0.wireOp",EDGE,"E117"),sQuery(id+"F0.wireOp",EDGE,"E118"),sQuery(id+"F0.wireOp",EDGE,"E119"),sQuery(id+"F0.wireOp",EDGE,"E120"),sQuery(id+"F0.wireOp",EDGE,"E121"),sQuery(id+"F0.wireOp",EDGE,"E122"),sQuery(id+"F0.wireOp",EDGE,"E123"),sQuery(id+"F0.wireOp",EDGE,"E124"),sQuery(id+"F0.wireOp",EDGE,"E125"),sQuery(id+"F0.wireOp",EDGE,"E126"),sQuery(id+"F0.wireOp",EDGE,"E127"),sQuery(id+"F0.wireOp",EDGE,"E128"),sQuery(id+"F0.wireOp",EDGE,"E129"),sQuery(id+"F0.wireOp",EDGE,"E130"),sQuery(id+"F0.wireOp",EDGE,"E131"),sQuery(id+"F0.wireOp",EDGE,"E132"),sQuery(id+"F0.wireOp",EDGE,"E133"),sQuery(id+"F0.wireOp",EDGE,"E134"),sQuery(id+"F0.wireOp",EDGE,"E135"),sQuery(id+"F0.wireOp",EDGE,"E136"),sQuery(id+"F0.wireOp",EDGE,"E137"),sQuery(id+"F0.wireOp",EDGE,"E138"),sQuery(id+"F0.wireOp",EDGE,"E139"),sQuery(id+"F0.wireOp",EDGE,"E140"),sQuery(id+"F0.wireOp",EDGE,"E141"),sQuery(id+"F0.wireOp",EDGE,"E142"),sQuery(id+"F0.wireOp",EDGE,"E143"),sQuery(id+"F0.wireOp",EDGE,"E144"),sQuery(id+"F0.wireOp",EDGE,"E145"),sQuery(id+"F0.wireOp",EDGE,"E146"),sQuery(id+"F0.wireOp",EDGE,"E147"),sQuery(id+"F0.wireOp",EDGE,"E148"),sQuery(id+"F0.wireOp",EDGE,"E149"),sQuery(id+"F0.wireOp",EDGE,"E150"),sQuery(id+"F0.wireOp",EDGE,"E151"),sQuery(id+"F0.wireOp",EDGE,"E152"),sQuery(id+"F0.wireOp",EDGE,"E153"),sQuery(id+"F0.wireOp",EDGE,"E154"),sQuery(id+"F0.wireOp",EDGE,"E155"),sQuery(id+"F0.wireOp",EDGE,"E156"),sQuery(id+"F0.wireOp",EDGE,"E157"),sQuery(id+"F0.wireOp",EDGE,"E158"),sQuery(id+"F0.wireOp",EDGE,"E159"),sQuery(id+"F0.wireOp",EDGE,"E160"),sQuery(id+"F0.wireOp",EDGE,"E161"),sQuery(id+"F0.wireOp",EDGE,"E162"),sQuery(id+"F0.wireOp",EDGE,"E163")])],"isStart":false});
            var sketch = newSketch(context, id + "F17", { "sketchPlane" : qUnion([Q0])});
            skCircle(sketch, "E183", {"center": v(35.04, 52.81) * mm, "radius": 0.58 * mm});
            skSolve(sketch);
        }
        {
            var Q0;
            Q0 = qSketchRegion(id + "F17", true);
            extrude(context, id + "F18", {"entities" : qUnion([Q0]), "operationType" : NewBodyOperationType.ADD, "oppositeDirection" : true, "depth" : 5.4 * mm, "offsetDistance" : 25 * mm});
        }
        {
            var Q0;
            Q0=makeQuery(id+"F2.opExtrude","CAP_FACE",FACE,{"disambiguationData":[OSD([sQuery(id+"F0.wireOp",EDGE,"E0"),sQuery(id+"F0.wireOp",EDGE,"E1"),sQuery(id+"F0.wireOp",EDGE,"E2"),sQuery(id+"F0.wireOp",EDGE,"E3"),sQuery(id+"F0.wireOp",EDGE,"E4"),sQuery(id+"F0.wireOp",EDGE,"E5"),sQuery(id+"F0.wireOp",EDGE,"E6"),sQuery(id+"F0.wireOp",EDGE,"E7"),sQuery(id+"F0.wireOp",EDGE,"E8"),sQuery(id+"F0.wireOp",EDGE,"E9"),sQuery(id+"F0.wireOp",EDGE,"E10"),sQuery(id+"F0.wireOp",EDGE,"E11"),sQuery(id+"F0.wireOp",EDGE,"E12"),sQuery(id+"F0.wireOp",EDGE,"E13"),sQuery(id+"F0.wireOp",EDGE,"E14"),sQuery(id+"F0.wireOp",EDGE,"E15"),sQuery(id+"F0.wireOp",EDGE,"E16"),sQuery(id+"F0.wireOp",EDGE,"E17"),sQuery(id+"F0.wireOp",EDGE,"E18"),sQuery(id+"F0.wireOp",EDGE,"E19"),sQuery(id+"F0.wireOp",EDGE,"E20"),sQuery(id+"F0.wireOp",EDGE,"E21"),sQuery(id+"F0.wireOp",EDGE,"E22"),sQuery(id+"F0.wireOp",EDGE,"E23"),sQuery(id+"F0.wireOp",EDGE,"E24"),sQuery(id+"F0.wireOp",EDGE,"E25"),sQuery(id+"F0.wireOp",EDGE,"E26"),sQuery(id+"F0.wireOp",EDGE,"E27"),sQuery(id+"F0.wireOp",EDGE,"E28"),sQuery(id+"F0.wireOp",EDGE,"E29"),sQuery(id+"F0.wireOp",EDGE,"E30"),sQuery(id+"F0.wireOp",EDGE,"E31"),sQuery(id+"F0.wireOp",EDGE,"E32"),sQuery(id+"F0.wireOp",EDGE,"E33"),sQuery(id+"F0.wireOp",EDGE,"E34"),sQuery(id+"F0.wireOp",EDGE,"E35"),sQuery(id+"F0.wireOp",EDGE,"E36"),sQuery(id+"F0.wireOp",EDGE,"E37"),sQuery(id+"F0.wireOp",EDGE,"E38"),sQuery(id+"F0.wireOp",EDGE,"E39"),sQuery(id+"F0.wireOp",EDGE,"E40"),sQuery(id+"F0.wireOp",EDGE,"E41"),sQuery(id+"F0.wireOp",EDGE,"E42"),sQuery(id+"F0.wireOp",EDGE,"E43"),sQuery(id+"F0.wireOp",EDGE,"E44"),sQuery(id+"F0.wireOp",EDGE,"E45"),sQuery(id+"F0.wireOp",EDGE,"E46"),sQuery(id+"F0.wireOp",EDGE,"E47"),sQuery(id+"F0.wireOp",EDGE,"E48"),sQuery(id+"F0.wireOp",EDGE,"E49"),sQuery(id+"F0.wireOp",EDGE,"E50"),sQuery(id+"F0.wireOp",EDGE,"E51"),sQuery(id+"F0.wireOp",EDGE,"E52"),sQuery(id+"F0.wireOp",EDGE,"E53"),sQuery(id+"F0.wireOp",EDGE,"E54"),sQuery(id+"F0.wireOp",EDGE,"E55"),sQuery(id+"F0.wireOp",EDGE,"E56"),sQuery(id+"F0.wireOp",EDGE,"E57"),sQuery(id+"F0.wireOp",EDGE,"E58"),sQuery(id+"F0.wireOp",EDGE,"E59"),sQuery(id+"F0.wireOp",EDGE,"E60"),sQuery(id+"F0.wireOp",EDGE,"E61"),sQuery(id+"F0.wireOp",EDGE,"E62"),sQuery(id+"F0.wireOp",EDGE,"E63"),sQuery(id+"F0.wireOp",EDGE,"E64"),sQuery(id+"F0.wireOp",EDGE,"E65"),sQuery(id+"F0.wireOp",EDGE,"E66"),sQuery(id+"F0.wireOp",EDGE,"E67"),sQuery(id+"F0.wireOp",EDGE,"E68"),sQuery(id+"F0.wireOp",EDGE,"E69"),sQuery(id+"F0.wireOp",EDGE,"E70"),sQuery(id+"F0.wireOp",EDGE,"E71"),sQuery(id+"F0.wireOp",EDGE,"E72"),sQuery(id+"F0.wireOp",EDGE,"E73"),sQuery(id+"F0.wireOp",EDGE,"E74"),sQuery(id+"F0.wireOp",EDGE,"E75"),sQuery(id+"F0.wireOp",EDGE,"E76"),sQuery(id+"F0.wireOp",EDGE,"E77"),sQuery(id+"F0.wireOp",EDGE,"E78"),sQuery(id+"F0.wireOp",EDGE,"E79"),sQuery(id+"F0.wireOp",EDGE,"E80"),sQuery(id+"F0.wireOp",EDGE,"E81"),sQuery(id+"F0.wireOp",EDGE,"E82"),sQuery(id+"F0.wireOp",EDGE,"E83"),sQuery(id+"F0.wireOp",EDGE,"E84"),sQuery(id+"F0.wireOp",EDGE,"E85"),sQuery(id+"F0.wireOp",EDGE,"E86"),sQuery(id+"F0.wireOp",EDGE,"E87"),sQuery(id+"F0.wireOp",EDGE,"E88"),sQuery(id+"F0.wireOp",EDGE,"E89"),sQuery(id+"F0.wireOp",EDGE,"E90"),sQuery(id+"F0.wireOp",EDGE,"E91"),sQuery(id+"F0.wireOp",EDGE,"E92"),sQuery(id+"F0.wireOp",EDGE,"E93"),sQuery(id+"F0.wireOp",EDGE,"E94"),sQuery(id+"F0.wireOp",EDGE,"E95"),sQuery(id+"F0.wireOp",EDGE,"E96"),sQuery(id+"F0.wireOp",EDGE,"E97"),sQuery(id+"F0.wireOp",EDGE,"E98"),sQuery(id+"F0.wireOp",EDGE,"E99"),sQuery(id+"F0.wireOp",EDGE,"E100"),sQuery(id+"F0.wireOp",EDGE,"E101"),sQuery(id+"F0.wireOp",EDGE,"E102"),sQuery(id+"F0.wireOp",EDGE,"E103"),sQuery(id+"F0.wireOp",EDGE,"E104"),sQuery(id+"F0.wireOp",EDGE,"E105"),sQuery(id+"F0.wireOp",EDGE,"E106"),sQuery(id+"F0.wireOp",EDGE,"E107"),sQuery(id+"F0.wireOp",EDGE,"E108"),sQuery(id+"F0.wireOp",EDGE,"E109"),sQuery(id+"F0.wireOp",EDGE,"E110"),sQuery(id+"F0.wireOp",EDGE,"E111"),sQuery(id+"F0.wireOp",EDGE,"E112"),sQuery(id+"F0.wireOp",EDGE,"E113"),sQuery(id+"F0.wireOp",EDGE,"E114"),sQuery(id+"F0.wireOp",EDGE,"E115"),sQuery(id+"F0.wireOp",EDGE,"E116"),sQuery(id+"F0.wireOp",EDGE,"E117"),sQuery(id+"F0.wireOp",EDGE,"E118"),sQuery(id+"F0.wireOp",EDGE,"E119"),sQuery(id+"F0.wireOp",EDGE,"E120"),sQuery(id+"F0.wireOp",EDGE,"E121"),sQuery(id+"F0.wireOp",EDGE,"E122"),sQuery(id+"F0.wireOp",EDGE,"E123"),sQuery(id+"F0.wireOp",EDGE,"E124"),sQuery(id+"F0.wireOp",EDGE,"E125"),sQuery(id+"F0.wireOp",EDGE,"E126"),sQuery(id+"F0.wireOp",EDGE,"E127"),sQuery(id+"F0.wireOp",EDGE,"E128"),sQuery(id+"F0.wireOp",EDGE,"E129"),sQuery(id+"F0.wireOp",EDGE,"E130"),sQuery(id+"F0.wireOp",EDGE,"E131"),sQuery(id+"F0.wireOp",EDGE,"E132"),sQuery(id+"F0.wireOp",EDGE,"E133"),sQuery(id+"F0.wireOp",EDGE,"E134"),sQuery(id+"F0.wireOp",EDGE,"E135"),sQuery(id+"F0.wireOp",EDGE,"E136"),sQuery(id+"F0.wireOp",EDGE,"E137"),sQuery(id+"F0.wireOp",EDGE,"E138"),sQuery(id+"F0.wireOp",EDGE,"E139"),sQuery(id+"F0.wireOp",EDGE,"E140"),sQuery(id+"F0.wireOp",EDGE,"E141"),sQuery(id+"F0.wireOp",EDGE,"E142"),sQuery(id+"F0.wireOp",EDGE,"E143"),sQuery(id+"F0.wireOp",EDGE,"E144"),sQuery(id+"F0.wireOp",EDGE,"E145"),sQuery(id+"F0.wireOp",EDGE,"E146"),sQuery(id+"F0.wireOp",EDGE,"E147"),sQuery(id+"F0.wireOp",EDGE,"E148"),sQuery(id+"F0.wireOp",EDGE,"E149"),sQuery(id+"F0.wireOp",EDGE,"E150"),sQuery(id+"F0.wireOp",EDGE,"E151"),sQuery(id+"F0.wireOp",EDGE,"E152"),sQuery(id+"F0.wireOp",EDGE,"E153"),sQuery(id+"F0.wireOp",EDGE,"E154"),sQuery(id+"F0.wireOp",EDGE,"E155"),sQuery(id+"F0.wireOp",EDGE,"E156"),sQuery(id+"F0.wireOp",EDGE,"E157"),sQuery(id+"F0.wireOp",EDGE,"E158"),sQuery(id+"F0.wireOp",EDGE,"E159"),sQuery(id+"F0.wireOp",EDGE,"E160"),sQuery(id+"F0.wireOp",EDGE,"E161"),sQuery(id+"F0.wireOp",EDGE,"E162"),sQuery(id+"F0.wireOp",EDGE,"E163")])],"isStart":false});
            var sketch = newSketch(context, id + "F19", { "sketchPlane" : qUnion([Q0])});
            skCircle(sketch, "E184", {"center": v(35.13, 52.2) * mm, "radius": 0.6 * mm});
            skSolve(sketch);
        }
        {
            var Q0;
            Q0 = qSketchRegion(id + "F19", true);
            extrude(context, id + "F20", {"entities" : qUnion([Q0]), "operationType" : NewBodyOperationType.REMOVE, "oppositeDirection" : true, "depth" : 8.5 * mm, "offsetDistance" : 25 * mm});
        }
        {
            var Q0;
            Q0=makeQuery(id+"F2.opExtrude","CAP_FACE",FACE,{"disambiguationData":[OSD([sQuery(id+"F0.wireOp",EDGE,"E0"),sQuery(id+"F0.wireOp",EDGE,"E1"),sQuery(id+"F0.wireOp",EDGE,"E2"),sQuery(id+"F0.wireOp",EDGE,"E3"),sQuery(id+"F0.wireOp",EDGE,"E4"),sQuery(id+"F0.wireOp",EDGE,"E5"),sQuery(id+"F0.wireOp",EDGE,"E6"),sQuery(id+"F0.wireOp",EDGE,"E7"),sQuery(id+"F0.wireOp",EDGE,"E8"),sQuery(id+"F0.wireOp",EDGE,"E9"),sQuery(id+"F0.wireOp",EDGE,"E10"),sQuery(id+"F0.wireOp",EDGE,"E11"),sQuery(id+"F0.wireOp",EDGE,"E12"),sQuery(id+"F0.wireOp",EDGE,"E13"),sQuery(id+"F0.wireOp",EDGE,"E14"),sQuery(id+"F0.wireOp",EDGE,"E15"),sQuery(id+"F0.wireOp",EDGE,"E16"),sQuery(id+"F0.wireOp",EDGE,"E17"),sQuery(id+"F0.wireOp",EDGE,"E18"),sQuery(id+"F0.wireOp",EDGE,"E19"),sQuery(id+"F0.wireOp",EDGE,"E20"),sQuery(id+"F0.wireOp",EDGE,"E21"),sQuery(id+"F0.wireOp",EDGE,"E22"),sQuery(id+"F0.wireOp",EDGE,"E23"),sQuery(id+"F0.wireOp",EDGE,"E24"),sQuery(id+"F0.wireOp",EDGE,"E25"),sQuery(id+"F0.wireOp",EDGE,"E26"),sQuery(id+"F0.wireOp",EDGE,"E27"),sQuery(id+"F0.wireOp",EDGE,"E28"),sQuery(id+"F0.wireOp",EDGE,"E29"),sQuery(id+"F0.wireOp",EDGE,"E30"),sQuery(id+"F0.wireOp",EDGE,"E31"),sQuery(id+"F0.wireOp",EDGE,"E32"),sQuery(id+"F0.wireOp",EDGE,"E33"),sQuery(id+"F0.wireOp",EDGE,"E34"),sQuery(id+"F0.wireOp",EDGE,"E35"),sQuery(id+"F0.wireOp",EDGE,"E36"),sQuery(id+"F0.wireOp",EDGE,"E37"),sQuery(id+"F0.wireOp",EDGE,"E38"),sQuery(id+"F0.wireOp",EDGE,"E39"),sQuery(id+"F0.wireOp",EDGE,"E40"),sQuery(id+"F0.wireOp",EDGE,"E41"),sQuery(id+"F0.wireOp",EDGE,"E42"),sQuery(id+"F0.wireOp",EDGE,"E43"),sQuery(id+"F0.wireOp",EDGE,"E44"),sQuery(id+"F0.wireOp",EDGE,"E45"),sQuery(id+"F0.wireOp",EDGE,"E46"),sQuery(id+"F0.wireOp",EDGE,"E47"),sQuery(id+"F0.wireOp",EDGE,"E48"),sQuery(id+"F0.wireOp",EDGE,"E49"),sQuery(id+"F0.wireOp",EDGE,"E50"),sQuery(id+"F0.wireOp",EDGE,"E51"),sQuery(id+"F0.wireOp",EDGE,"E52"),sQuery(id+"F0.wireOp",EDGE,"E53"),sQuery(id+"F0.wireOp",EDGE,"E54"),sQuery(id+"F0.wireOp",EDGE,"E55"),sQuery(id+"F0.wireOp",EDGE,"E56"),sQuery(id+"F0.wireOp",EDGE,"E57"),sQuery(id+"F0.wireOp",EDGE,"E58"),sQuery(id+"F0.wireOp",EDGE,"E59"),sQuery(id+"F0.wireOp",EDGE,"E60"),sQuery(id+"F0.wireOp",EDGE,"E61"),sQuery(id+"F0.wireOp",EDGE,"E62"),sQuery(id+"F0.wireOp",EDGE,"E63"),sQuery(id+"F0.wireOp",EDGE,"E64"),sQuery(id+"F0.wireOp",EDGE,"E65"),sQuery(id+"F0.wireOp",EDGE,"E66"),sQuery(id+"F0.wireOp",EDGE,"E67"),sQuery(id+"F0.wireOp",EDGE,"E68"),sQuery(id+"F0.wireOp",EDGE,"E69"),sQuery(id+"F0.wireOp",EDGE,"E70"),sQuery(id+"F0.wireOp",EDGE,"E71"),sQuery(id+"F0.wireOp",EDGE,"E72"),sQuery(id+"F0.wireOp",EDGE,"E73"),sQuery(id+"F0.wireOp",EDGE,"E74"),sQuery(id+"F0.wireOp",EDGE,"E75"),sQuery(id+"F0.wireOp",EDGE,"E76"),sQuery(id+"F0.wireOp",EDGE,"E77"),sQuery(id+"F0.wireOp",EDGE,"E78"),sQuery(id+"F0.wireOp",EDGE,"E79"),sQuery(id+"F0.wireOp",EDGE,"E80"),sQuery(id+"F0.wireOp",EDGE,"E81"),sQuery(id+"F0.wireOp",EDGE,"E82"),sQuery(id+"F0.wireOp",EDGE,"E83"),sQuery(id+"F0.wireOp",EDGE,"E84"),sQuery(id+"F0.wireOp",EDGE,"E85"),sQuery(id+"F0.wireOp",EDGE,"E86"),sQuery(id+"F0.wireOp",EDGE,"E87"),sQuery(id+"F0.wireOp",EDGE,"E88"),sQuery(id+"F0.wireOp",EDGE,"E89"),sQuery(id+"F0.wireOp",EDGE,"E90"),sQuery(id+"F0.wireOp",EDGE,"E91"),sQuery(id+"F0.wireOp",EDGE,"E92"),sQuery(id+"F0.wireOp",EDGE,"E93"),sQuery(id+"F0.wireOp",EDGE,"E94"),sQuery(id+"F0.wireOp",EDGE,"E95"),sQuery(id+"F0.wireOp",EDGE,"E96"),sQuery(id+"F0.wireOp",EDGE,"E97"),sQuery(id+"F0.wireOp",EDGE,"E98"),sQuery(id+"F0.wireOp",EDGE,"E99"),sQuery(id+"F0.wireOp",EDGE,"E100"),sQuery(id+"F0.wireOp",EDGE,"E101"),sQuery(id+"F0.wireOp",EDGE,"E102"),sQuery(id+"F0.wireOp",EDGE,"E103"),sQuery(id+"F0.wireOp",EDGE,"E104"),sQuery(id+"F0.wireOp",EDGE,"E105"),sQuery(id+"F0.wireOp",EDGE,"E106"),sQuery(id+"F0.wireOp",EDGE,"E107"),sQuery(id+"F0.wireOp",EDGE,"E108"),sQuery(id+"F0.wireOp",EDGE,"E109"),sQuery(id+"F0.wireOp",EDGE,"E110"),sQuery(id+"F0.wireOp",EDGE,"E111"),sQuery(id+"F0.wireOp",EDGE,"E112"),sQuery(id+"F0.wireOp",EDGE,"E113"),sQuery(id+"F0.wireOp",EDGE,"E114"),sQuery(id+"F0.wireOp",EDGE,"E115"),sQuery(id+"F0.wireOp",EDGE,"E116"),sQuery(id+"F0.wireOp",EDGE,"E117"),sQuery(id+"F0.wireOp",EDGE,"E118"),sQuery(id+"F0.wireOp",EDGE,"E119"),sQuery(id+"F0.wireOp",EDGE,"E120"),sQuery(id+"F0.wireOp",EDGE,"E121"),sQuery(id+"F0.wireOp",EDGE,"E122"),sQuery(id+"F0.wireOp",EDGE,"E123"),sQuery(id+"F0.wireOp",EDGE,"E124"),sQuery(id+"F0.wireOp",EDGE,"E125"),sQuery(id+"F0.wireOp",EDGE,"E126"),sQuery(id+"F0.wireOp",EDGE,"E127"),sQuery(id+"F0.wireOp",EDGE,"E128"),sQuery(id+"F0.wireOp",EDGE,"E129"),sQuery(id+"F0.wireOp",EDGE,"E130"),sQuery(id+"F0.wireOp",EDGE,"E131"),sQuery(id+"F0.wireOp",EDGE,"E132"),sQuery(id+"F0.wireOp",EDGE,"E133"),sQuery(id+"F0.wireOp",EDGE,"E134"),sQuery(id+"F0.wireOp",EDGE,"E135"),sQuery(id+"F0.wireOp",EDGE,"E136"),sQuery(id+"F0.wireOp",EDGE,"E137"),sQuery(id+"F0.wireOp",EDGE,"E138"),sQuery(id+"F0.wireOp",EDGE,"E139"),sQuery(id+"F0.wireOp",EDGE,"E140"),sQuery(id+"F0.wireOp",EDGE,"E141"),sQuery(id+"F0.wireOp",EDGE,"E142"),sQuery(id+"F0.wireOp",EDGE,"E143"),sQuery(id+"F0.wireOp",EDGE,"E144"),sQuery(id+"F0.wireOp",EDGE,"E145"),sQuery(id+"F0.wireOp",EDGE,"E146"),sQuery(id+"F0.wireOp",EDGE,"E147"),sQuery(id+"F0.wireOp",EDGE,"E148"),sQuery(id+"F0.wireOp",EDGE,"E149"),sQuery(id+"F0.wireOp",EDGE,"E150"),sQuery(id+"F0.wireOp",EDGE,"E151"),sQuery(id+"F0.wireOp",EDGE,"E152"),sQuery(id+"F0.wireOp",EDGE,"E153"),sQuery(id+"F0.wireOp",EDGE,"E154"),sQuery(id+"F0.wireOp",EDGE,"E155"),sQuery(id+"F0.wireOp",EDGE,"E156"),sQuery(id+"F0.wireOp",EDGE,"E157"),sQuery(id+"F0.wireOp",EDGE,"E158"),sQuery(id+"F0.wireOp",EDGE,"E159"),sQuery(id+"F0.wireOp",EDGE,"E160"),sQuery(id+"F0.wireOp",EDGE,"E161"),sQuery(id+"F0.wireOp",EDGE,"E162"),sQuery(id+"F0.wireOp",EDGE,"E163")])],"isStart":false});
            var sketch = newSketch(context, id + "F21", { "sketchPlane" : qUnion([Q0])});
            skCircle(sketch, "E185", {"center": v(35.84, 50.18) * mm, "radius": 0.62 * mm});
            skSolve(sketch);
        }
        {
            var Q0;
            Q0 = qSketchRegion(id + "F21", true);
            extrude(context, id + "F22", {"entities" : qUnion([Q0]), "operationType" : NewBodyOperationType.REMOVE, "oppositeDirection" : true, "depth" : 3.8 * mm, "offsetDistance" : 25 * mm});
        }
        {
            var Q0;
            Q0=makeQuery(id+"F2.opExtrude","CAP_FACE",FACE,{"disambiguationData":[OSD([sQuery(id+"F0.wireOp",EDGE,"E0"),sQuery(id+"F0.wireOp",EDGE,"E1"),sQuery(id+"F0.wireOp",EDGE,"E2"),sQuery(id+"F0.wireOp",EDGE,"E3"),sQuery(id+"F0.wireOp",EDGE,"E4"),sQuery(id+"F0.wireOp",EDGE,"E5"),sQuery(id+"F0.wireOp",EDGE,"E6"),sQuery(id+"F0.wireOp",EDGE,"E7"),sQuery(id+"F0.wireOp",EDGE,"E8"),sQuery(id+"F0.wireOp",EDGE,"E9"),sQuery(id+"F0.wireOp",EDGE,"E10"),sQuery(id+"F0.wireOp",EDGE,"E11"),sQuery(id+"F0.wireOp",EDGE,"E12"),sQuery(id+"F0.wireOp",EDGE,"E13"),sQuery(id+"F0.wireOp",EDGE,"E14"),sQuery(id+"F0.wireOp",EDGE,"E15"),sQuery(id+"F0.wireOp",EDGE,"E16"),sQuery(id+"F0.wireOp",EDGE,"E17"),sQuery(id+"F0.wireOp",EDGE,"E18"),sQuery(id+"F0.wireOp",EDGE,"E19"),sQuery(id+"F0.wireOp",EDGE,"E20"),sQuery(id+"F0.wireOp",EDGE,"E21"),sQuery(id+"F0.wireOp",EDGE,"E22"),sQuery(id+"F0.wireOp",EDGE,"E23"),sQuery(id+"F0.wireOp",EDGE,"E24"),sQuery(id+"F0.wireOp",EDGE,"E25"),sQuery(id+"F0.wireOp",EDGE,"E26"),sQuery(id+"F0.wireOp",EDGE,"E27"),sQuery(id+"F0.wireOp",EDGE,"E28"),sQuery(id+"F0.wireOp",EDGE,"E29"),sQuery(id+"F0.wireOp",EDGE,"E30"),sQuery(id+"F0.wireOp",EDGE,"E31"),sQuery(id+"F0.wireOp",EDGE,"E32"),sQuery(id+"F0.wireOp",EDGE,"E33"),sQuery(id+"F0.wireOp",EDGE,"E34"),sQuery(id+"F0.wireOp",EDGE,"E35"),sQuery(id+"F0.wireOp",EDGE,"E36"),sQuery(id+"F0.wireOp",EDGE,"E37"),sQuery(id+"F0.wireOp",EDGE,"E38"),sQuery(id+"F0.wireOp",EDGE,"E39"),sQuery(id+"F0.wireOp",EDGE,"E40"),sQuery(id+"F0.wireOp",EDGE,"E41"),sQuery(id+"F0.wireOp",EDGE,"E42"),sQuery(id+"F0.wireOp",EDGE,"E43"),sQuery(id+"F0.wireOp",EDGE,"E44"),sQuery(id+"F0.wireOp",EDGE,"E45"),sQuery(id+"F0.wireOp",EDGE,"E46"),sQuery(id+"F0.wireOp",EDGE,"E47"),sQuery(id+"F0.wireOp",EDGE,"E48"),sQuery(id+"F0.wireOp",EDGE,"E49"),sQuery(id+"F0.wireOp",EDGE,"E50"),sQuery(id+"F0.wireOp",EDGE,"E51"),sQuery(id+"F0.wireOp",EDGE,"E52"),sQuery(id+"F0.wireOp",EDGE,"E53"),sQuery(id+"F0.wireOp",EDGE,"E54"),sQuery(id+"F0.wireOp",EDGE,"E55"),sQuery(id+"F0.wireOp",EDGE,"E56"),sQuery(id+"F0.wireOp",EDGE,"E57"),sQuery(id+"F0.wireOp",EDGE,"E58"),sQuery(id+"F0.wireOp",EDGE,"E59"),sQuery(id+"F0.wireOp",EDGE,"E60"),sQuery(id+"F0.wireOp",EDGE,"E61"),sQuery(id+"F0.wireOp",EDGE,"E62"),sQuery(id+"F0.wireOp",EDGE,"E63"),sQuery(id+"F0.wireOp",EDGE,"E64"),sQuery(id+"F0.wireOp",EDGE,"E65"),sQuery(id+"F0.wireOp",EDGE,"E66"),sQuery(id+"F0.wireOp",EDGE,"E67"),sQuery(id+"F0.wireOp",EDGE,"E68"),sQuery(id+"F0.wireOp",EDGE,"E69"),sQuery(id+"F0.wireOp",EDGE,"E70"),sQuery(id+"F0.wireOp",EDGE,"E71"),sQuery(id+"F0.wireOp",EDGE,"E72"),sQuery(id+"F0.wireOp",EDGE,"E73"),sQuery(id+"F0.wireOp",EDGE,"E74"),sQuery(id+"F0.wireOp",EDGE,"E75"),sQuery(id+"F0.wireOp",EDGE,"E76"),sQuery(id+"F0.wireOp",EDGE,"E77"),sQuery(id+"F0.wireOp",EDGE,"E78"),sQuery(id+"F0.wireOp",EDGE,"E79"),sQuery(id+"F0.wireOp",EDGE,"E80"),sQuery(id+"F0.wireOp",EDGE,"E81"),sQuery(id+"F0.wireOp",EDGE,"E82"),sQuery(id+"F0.wireOp",EDGE,"E83"),sQuery(id+"F0.wireOp",EDGE,"E84"),sQuery(id+"F0.wireOp",EDGE,"E85"),sQuery(id+"F0.wireOp",EDGE,"E86"),sQuery(id+"F0.wireOp",EDGE,"E87"),sQuery(id+"F0.wireOp",EDGE,"E88"),sQuery(id+"F0.wireOp",EDGE,"E89"),sQuery(id+"F0.wireOp",EDGE,"E90"),sQuery(id+"F0.wireOp",EDGE,"E91"),sQuery(id+"F0.wireOp",EDGE,"E92"),sQuery(id+"F0.wireOp",EDGE,"E93"),sQuery(id+"F0.wireOp",EDGE,"E94"),sQuery(id+"F0.wireOp",EDGE,"E95"),sQuery(id+"F0.wireOp",EDGE,"E96"),sQuery(id+"F0.wireOp",EDGE,"E97"),sQuery(id+"F0.wireOp",EDGE,"E98"),sQuery(id+"F0.wireOp",EDGE,"E99"),sQuery(id+"F0.wireOp",EDGE,"E100"),sQuery(id+"F0.wireOp",EDGE,"E101"),sQuery(id+"F0.wireOp",EDGE,"E102"),sQuery(id+"F0.wireOp",EDGE,"E103"),sQuery(id+"F0.wireOp",EDGE,"E104"),sQuery(id+"F0.wireOp",EDGE,"E105"),sQuery(id+"F0.wireOp",EDGE,"E106"),sQuery(id+"F0.wireOp",EDGE,"E107"),sQuery(id+"F0.wireOp",EDGE,"E108"),sQuery(id+"F0.wireOp",EDGE,"E109"),sQuery(id+"F0.wireOp",EDGE,"E110"),sQuery(id+"F0.wireOp",EDGE,"E111"),sQuery(id+"F0.wireOp",EDGE,"E112"),sQuery(id+"F0.wireOp",EDGE,"E113"),sQuery(id+"F0.wireOp",EDGE,"E114"),sQuery(id+"F0.wireOp",EDGE,"E115"),sQuery(id+"F0.wireOp",EDGE,"E116"),sQuery(id+"F0.wireOp",EDGE,"E117"),sQuery(id+"F0.wireOp",EDGE,"E118"),sQuery(id+"F0.wireOp",EDGE,"E119"),sQuery(id+"F0.wireOp",EDGE,"E120"),sQuery(id+"F0.wireOp",EDGE,"E121"),sQuery(id+"F0.wireOp",EDGE,"E122"),sQuery(id+"F0.wireOp",EDGE,"E123"),sQuery(id+"F0.wireOp",EDGE,"E124"),sQuery(id+"F0.wireOp",EDGE,"E125"),sQuery(id+"F0.wireOp",EDGE,"E126"),sQuery(id+"F0.wireOp",EDGE,"E127"),sQuery(id+"F0.wireOp",EDGE,"E128"),sQuery(id+"F0.wireOp",EDGE,"E129"),sQuery(id+"F0.wireOp",EDGE,"E130"),sQuery(id+"F0.wireOp",EDGE,"E131"),sQuery(id+"F0.wireOp",EDGE,"E132"),sQuery(id+"F0.wireOp",EDGE,"E133"),sQuery(id+"F0.wireOp",EDGE,"E134"),sQuery(id+"F0.wireOp",EDGE,"E135"),sQuery(id+"F0.wireOp",EDGE,"E136"),sQuery(id+"F0.wireOp",EDGE,"E137"),sQuery(id+"F0.wireOp",EDGE,"E138"),sQuery(id+"F0.wireOp",EDGE,"E139"),sQuery(id+"F0.wireOp",EDGE,"E140"),sQuery(id+"F0.wireOp",EDGE,"E141"),sQuery(id+"F0.wireOp",EDGE,"E142"),sQuery(id+"F0.wireOp",EDGE,"E143"),sQuery(id+"F0.wireOp",EDGE,"E144"),sQuery(id+"F0.wireOp",EDGE,"E145"),sQuery(id+"F0.wireOp",EDGE,"E146"),sQuery(id+"F0.wireOp",EDGE,"E147"),sQuery(id+"F0.wireOp",EDGE,"E148"),sQuery(id+"F0.wireOp",EDGE,"E149"),sQuery(id+"F0.wireOp",EDGE,"E150"),sQuery(id+"F0.wireOp",EDGE,"E151"),sQuery(id+"F0.wireOp",EDGE,"E152"),sQuery(id+"F0.wireOp",EDGE,"E153"),sQuery(id+"F0.wireOp",EDGE,"E154"),sQuery(id+"F0.wireOp",EDGE,"E155"),sQuery(id+"F0.wireOp",EDGE,"E156"),sQuery(id+"F0.wireOp",EDGE,"E157"),sQuery(id+"F0.wireOp",EDGE,"E158"),sQuery(id+"F0.wireOp",EDGE,"E159"),sQuery(id+"F0.wireOp",EDGE,"E160"),sQuery(id+"F0.wireOp",EDGE,"E161"),sQuery(id+"F0.wireOp",EDGE,"E162"),sQuery(id+"F0.wireOp",EDGE,"E163")])],"isStart":false});
            var sketch = newSketch(context, id + "F23", { "sketchPlane" : qUnion([Q0])});
            skCircle(sketch, "E186", {"center": v(36.74, 48.13) * mm, "radius": 0.62 * mm});
            skSolve(sketch);
        }
        {
            var Q0;
            Q0 = qSketchRegion(id + "F23", true);
            extrude(context, id + "F24", {"entities" : qUnion([Q0]), "operationType" : NewBodyOperationType.REMOVE, "oppositeDirection" : true, "depth" : 3.8 * mm, "offsetDistance" : 25 * mm});
        }
        {
            var Q0;
            Q0=makeQuery(id+"F2.opExtrude","CAP_FACE",FACE,{"disambiguationData":[OSD([sQuery(id+"F0.wireOp",EDGE,"E0"),sQuery(id+"F0.wireOp",EDGE,"E1"),sQuery(id+"F0.wireOp",EDGE,"E2"),sQuery(id+"F0.wireOp",EDGE,"E3"),sQuery(id+"F0.wireOp",EDGE,"E4"),sQuery(id+"F0.wireOp",EDGE,"E5"),sQuery(id+"F0.wireOp",EDGE,"E6"),sQuery(id+"F0.wireOp",EDGE,"E7"),sQuery(id+"F0.wireOp",EDGE,"E8"),sQuery(id+"F0.wireOp",EDGE,"E9"),sQuery(id+"F0.wireOp",EDGE,"E10"),sQuery(id+"F0.wireOp",EDGE,"E11"),sQuery(id+"F0.wireOp",EDGE,"E12"),sQuery(id+"F0.wireOp",EDGE,"E13"),sQuery(id+"F0.wireOp",EDGE,"E14"),sQuery(id+"F0.wireOp",EDGE,"E15"),sQuery(id+"F0.wireOp",EDGE,"E16"),sQuery(id+"F0.wireOp",EDGE,"E17"),sQuery(id+"F0.wireOp",EDGE,"E18"),sQuery(id+"F0.wireOp",EDGE,"E19"),sQuery(id+"F0.wireOp",EDGE,"E20"),sQuery(id+"F0.wireOp",EDGE,"E21"),sQuery(id+"F0.wireOp",EDGE,"E22"),sQuery(id+"F0.wireOp",EDGE,"E23"),sQuery(id+"F0.wireOp",EDGE,"E24"),sQuery(id+"F0.wireOp",EDGE,"E25"),sQuery(id+"F0.wireOp",EDGE,"E26"),sQuery(id+"F0.wireOp",EDGE,"E27"),sQuery(id+"F0.wireOp",EDGE,"E28"),sQuery(id+"F0.wireOp",EDGE,"E29"),sQuery(id+"F0.wireOp",EDGE,"E30"),sQuery(id+"F0.wireOp",EDGE,"E31"),sQuery(id+"F0.wireOp",EDGE,"E32"),sQuery(id+"F0.wireOp",EDGE,"E33"),sQuery(id+"F0.wireOp",EDGE,"E34"),sQuery(id+"F0.wireOp",EDGE,"E35"),sQuery(id+"F0.wireOp",EDGE,"E36"),sQuery(id+"F0.wireOp",EDGE,"E37"),sQuery(id+"F0.wireOp",EDGE,"E38"),sQuery(id+"F0.wireOp",EDGE,"E39"),sQuery(id+"F0.wireOp",EDGE,"E40"),sQuery(id+"F0.wireOp",EDGE,"E41"),sQuery(id+"F0.wireOp",EDGE,"E42"),sQuery(id+"F0.wireOp",EDGE,"E43"),sQuery(id+"F0.wireOp",EDGE,"E44"),sQuery(id+"F0.wireOp",EDGE,"E45"),sQuery(id+"F0.wireOp",EDGE,"E46"),sQuery(id+"F0.wireOp",EDGE,"E47"),sQuery(id+"F0.wireOp",EDGE,"E48"),sQuery(id+"F0.wireOp",EDGE,"E49"),sQuery(id+"F0.wireOp",EDGE,"E50"),sQuery(id+"F0.wireOp",EDGE,"E51"),sQuery(id+"F0.wireOp",EDGE,"E52"),sQuery(id+"F0.wireOp",EDGE,"E53"),sQuery(id+"F0.wireOp",EDGE,"E54"),sQuery(id+"F0.wireOp",EDGE,"E55"),sQuery(id+"F0.wireOp",EDGE,"E56"),sQuery(id+"F0.wireOp",EDGE,"E57"),sQuery(id+"F0.wireOp",EDGE,"E58"),sQuery(id+"F0.wireOp",EDGE,"E59"),sQuery(id+"F0.wireOp",EDGE,"E60"),sQuery(id+"F0.wireOp",EDGE,"E61"),sQuery(id+"F0.wireOp",EDGE,"E62"),sQuery(id+"F0.wireOp",EDGE,"E63"),sQuery(id+"F0.wireOp",EDGE,"E64"),sQuery(id+"F0.wireOp",EDGE,"E65"),sQuery(id+"F0.wireOp",EDGE,"E66"),sQuery(id+"F0.wireOp",EDGE,"E67"),sQuery(id+"F0.wireOp",EDGE,"E68"),sQuery(id+"F0.wireOp",EDGE,"E69"),sQuery(id+"F0.wireOp",EDGE,"E70"),sQuery(id+"F0.wireOp",EDGE,"E71"),sQuery(id+"F0.wireOp",EDGE,"E72"),sQuery(id+"F0.wireOp",EDGE,"E73"),sQuery(id+"F0.wireOp",EDGE,"E74"),sQuery(id+"F0.wireOp",EDGE,"E75"),sQuery(id+"F0.wireOp",EDGE,"E76"),sQuery(id+"F0.wireOp",EDGE,"E77"),sQuery(id+"F0.wireOp",EDGE,"E78"),sQuery(id+"F0.wireOp",EDGE,"E79"),sQuery(id+"F0.wireOp",EDGE,"E80"),sQuery(id+"F0.wireOp",EDGE,"E81"),sQuery(id+"F0.wireOp",EDGE,"E82"),sQuery(id+"F0.wireOp",EDGE,"E83"),sQuery(id+"F0.wireOp",EDGE,"E84"),sQuery(id+"F0.wireOp",EDGE,"E85"),sQuery(id+"F0.wireOp",EDGE,"E86"),sQuery(id+"F0.wireOp",EDGE,"E87"),sQuery(id+"F0.wireOp",EDGE,"E88"),sQuery(id+"F0.wireOp",EDGE,"E89"),sQuery(id+"F0.wireOp",EDGE,"E90"),sQuery(id+"F0.wireOp",EDGE,"E91"),sQuery(id+"F0.wireOp",EDGE,"E92"),sQuery(id+"F0.wireOp",EDGE,"E93"),sQuery(id+"F0.wireOp",EDGE,"E94"),sQuery(id+"F0.wireOp",EDGE,"E95"),sQuery(id+"F0.wireOp",EDGE,"E96"),sQuery(id+"F0.wireOp",EDGE,"E97"),sQuery(id+"F0.wireOp",EDGE,"E98"),sQuery(id+"F0.wireOp",EDGE,"E99"),sQuery(id+"F0.wireOp",EDGE,"E100"),sQuery(id+"F0.wireOp",EDGE,"E101"),sQuery(id+"F0.wireOp",EDGE,"E102"),sQuery(id+"F0.wireOp",EDGE,"E103"),sQuery(id+"F0.wireOp",EDGE,"E104"),sQuery(id+"F0.wireOp",EDGE,"E105"),sQuery(id+"F0.wireOp",EDGE,"E106"),sQuery(id+"F0.wireOp",EDGE,"E107"),sQuery(id+"F0.wireOp",EDGE,"E108"),sQuery(id+"F0.wireOp",EDGE,"E109"),sQuery(id+"F0.wireOp",EDGE,"E110"),sQuery(id+"F0.wireOp",EDGE,"E111"),sQuery(id+"F0.wireOp",EDGE,"E112"),sQuery(id+"F0.wireOp",EDGE,"E113"),sQuery(id+"F0.wireOp",EDGE,"E114"),sQuery(id+"F0.wireOp",EDGE,"E115"),sQuery(id+"F0.wireOp",EDGE,"E116"),sQuery(id+"F0.wireOp",EDGE,"E117"),sQuery(id+"F0.wireOp",EDGE,"E118"),sQuery(id+"F0.wireOp",EDGE,"E119"),sQuery(id+"F0.wireOp",EDGE,"E120"),sQuery(id+"F0.wireOp",EDGE,"E121"),sQuery(id+"F0.wireOp",EDGE,"E122"),sQuery(id+"F0.wireOp",EDGE,"E123"),sQuery(id+"F0.wireOp",EDGE,"E124"),sQuery(id+"F0.wireOp",EDGE,"E125"),sQuery(id+"F0.wireOp",EDGE,"E126"),sQuery(id+"F0.wireOp",EDGE,"E127"),sQuery(id+"F0.wireOp",EDGE,"E128"),sQuery(id+"F0.wireOp",EDGE,"E129"),sQuery(id+"F0.wireOp",EDGE,"E130"),sQuery(id+"F0.wireOp",EDGE,"E131"),sQuery(id+"F0.wireOp",EDGE,"E132"),sQuery(id+"F0.wireOp",EDGE,"E133"),sQuery(id+"F0.wireOp",EDGE,"E134"),sQuery(id+"F0.wireOp",EDGE,"E135"),sQuery(id+"F0.wireOp",EDGE,"E136"),sQuery(id+"F0.wireOp",EDGE,"E137"),sQuery(id+"F0.wireOp",EDGE,"E138"),sQuery(id+"F0.wireOp",EDGE,"E139"),sQuery(id+"F0.wireOp",EDGE,"E140"),sQuery(id+"F0.wireOp",EDGE,"E141"),sQuery(id+"F0.wireOp",EDGE,"E142"),sQuery(id+"F0.wireOp",EDGE,"E143"),sQuery(id+"F0.wireOp",EDGE,"E144"),sQuery(id+"F0.wireOp",EDGE,"E145"),sQuery(id+"F0.wireOp",EDGE,"E146"),sQuery(id+"F0.wireOp",EDGE,"E147"),sQuery(id+"F0.wireOp",EDGE,"E148"),sQuery(id+"F0.wireOp",EDGE,"E149"),sQuery(id+"F0.wireOp",EDGE,"E150"),sQuery(id+"F0.wireOp",EDGE,"E151"),sQuery(id+"F0.wireOp",EDGE,"E152"),sQuery(id+"F0.wireOp",EDGE,"E153"),sQuery(id+"F0.wireOp",EDGE,"E154"),sQuery(id+"F0.wireOp",EDGE,"E155"),sQuery(id+"F0.wireOp",EDGE,"E156"),sQuery(id+"F0.wireOp",EDGE,"E157"),sQuery(id+"F0.wireOp",EDGE,"E158"),sQuery(id+"F0.wireOp",EDGE,"E159"),sQuery(id+"F0.wireOp",EDGE,"E160"),sQuery(id+"F0.wireOp",EDGE,"E161"),sQuery(id+"F0.wireOp",EDGE,"E162"),sQuery(id+"F0.wireOp",EDGE,"E163")])],"isStart":false});
            var sketch = newSketch(context, id + "F25", { "sketchPlane" : qUnion([Q0])});
            skCircle(sketch, "E187", {"center": v(37.94, 46.46) * mm, "radius": 0.55 * mm});
            skSolve(sketch);
        }
        {
            var Q0;
            Q0 = qSketchRegion(id + "F25", true);
            extrude(context, id + "F26", {"entities" : qUnion([Q0]), "operationType" : NewBodyOperationType.REMOVE, "oppositeDirection" : true, "depth" : 3.8 * mm, "offsetDistance" : 25 * mm});
        }
        {
            var Q0;
            Q0=makeQuery(id+"F2.opExtrude","CAP_FACE",FACE,{"disambiguationData":[OSD([sQuery(id+"F0.wireOp",EDGE,"E0"),sQuery(id+"F0.wireOp",EDGE,"E1"),sQuery(id+"F0.wireOp",EDGE,"E2"),sQuery(id+"F0.wireOp",EDGE,"E3"),sQuery(id+"F0.wireOp",EDGE,"E4"),sQuery(id+"F0.wireOp",EDGE,"E5"),sQuery(id+"F0.wireOp",EDGE,"E6"),sQuery(id+"F0.wireOp",EDGE,"E7"),sQuery(id+"F0.wireOp",EDGE,"E8"),sQuery(id+"F0.wireOp",EDGE,"E9"),sQuery(id+"F0.wireOp",EDGE,"E10"),sQuery(id+"F0.wireOp",EDGE,"E11"),sQuery(id+"F0.wireOp",EDGE,"E12"),sQuery(id+"F0.wireOp",EDGE,"E13"),sQuery(id+"F0.wireOp",EDGE,"E14"),sQuery(id+"F0.wireOp",EDGE,"E15"),sQuery(id+"F0.wireOp",EDGE,"E16"),sQuery(id+"F0.wireOp",EDGE,"E17"),sQuery(id+"F0.wireOp",EDGE,"E18"),sQuery(id+"F0.wireOp",EDGE,"E19"),sQuery(id+"F0.wireOp",EDGE,"E20"),sQuery(id+"F0.wireOp",EDGE,"E21"),sQuery(id+"F0.wireOp",EDGE,"E22"),sQuery(id+"F0.wireOp",EDGE,"E23"),sQuery(id+"F0.wireOp",EDGE,"E24"),sQuery(id+"F0.wireOp",EDGE,"E25"),sQuery(id+"F0.wireOp",EDGE,"E26"),sQuery(id+"F0.wireOp",EDGE,"E27"),sQuery(id+"F0.wireOp",EDGE,"E28"),sQuery(id+"F0.wireOp",EDGE,"E29"),sQuery(id+"F0.wireOp",EDGE,"E30"),sQuery(id+"F0.wireOp",EDGE,"E31"),sQuery(id+"F0.wireOp",EDGE,"E32"),sQuery(id+"F0.wireOp",EDGE,"E33"),sQuery(id+"F0.wireOp",EDGE,"E34"),sQuery(id+"F0.wireOp",EDGE,"E35"),sQuery(id+"F0.wireOp",EDGE,"E36"),sQuery(id+"F0.wireOp",EDGE,"E37"),sQuery(id+"F0.wireOp",EDGE,"E38"),sQuery(id+"F0.wireOp",EDGE,"E39"),sQuery(id+"F0.wireOp",EDGE,"E40"),sQuery(id+"F0.wireOp",EDGE,"E41"),sQuery(id+"F0.wireOp",EDGE,"E42"),sQuery(id+"F0.wireOp",EDGE,"E43"),sQuery(id+"F0.wireOp",EDGE,"E44"),sQuery(id+"F0.wireOp",EDGE,"E45"),sQuery(id+"F0.wireOp",EDGE,"E46"),sQuery(id+"F0.wireOp",EDGE,"E47"),sQuery(id+"F0.wireOp",EDGE,"E48"),sQuery(id+"F0.wireOp",EDGE,"E49"),sQuery(id+"F0.wireOp",EDGE,"E50"),sQuery(id+"F0.wireOp",EDGE,"E51"),sQuery(id+"F0.wireOp",EDGE,"E52"),sQuery(id+"F0.wireOp",EDGE,"E53"),sQuery(id+"F0.wireOp",EDGE,"E54"),sQuery(id+"F0.wireOp",EDGE,"E55"),sQuery(id+"F0.wireOp",EDGE,"E56"),sQuery(id+"F0.wireOp",EDGE,"E57"),sQuery(id+"F0.wireOp",EDGE,"E58"),sQuery(id+"F0.wireOp",EDGE,"E59"),sQuery(id+"F0.wireOp",EDGE,"E60"),sQuery(id+"F0.wireOp",EDGE,"E61"),sQuery(id+"F0.wireOp",EDGE,"E62"),sQuery(id+"F0.wireOp",EDGE,"E63"),sQuery(id+"F0.wireOp",EDGE,"E64"),sQuery(id+"F0.wireOp",EDGE,"E65"),sQuery(id+"F0.wireOp",EDGE,"E66"),sQuery(id+"F0.wireOp",EDGE,"E67"),sQuery(id+"F0.wireOp",EDGE,"E68"),sQuery(id+"F0.wireOp",EDGE,"E69"),sQuery(id+"F0.wireOp",EDGE,"E70"),sQuery(id+"F0.wireOp",EDGE,"E71"),sQuery(id+"F0.wireOp",EDGE,"E72"),sQuery(id+"F0.wireOp",EDGE,"E73"),sQuery(id+"F0.wireOp",EDGE,"E74"),sQuery(id+"F0.wireOp",EDGE,"E75"),sQuery(id+"F0.wireOp",EDGE,"E76"),sQuery(id+"F0.wireOp",EDGE,"E77"),sQuery(id+"F0.wireOp",EDGE,"E78"),sQuery(id+"F0.wireOp",EDGE,"E79"),sQuery(id+"F0.wireOp",EDGE,"E80"),sQuery(id+"F0.wireOp",EDGE,"E81"),sQuery(id+"F0.wireOp",EDGE,"E82"),sQuery(id+"F0.wireOp",EDGE,"E83"),sQuery(id+"F0.wireOp",EDGE,"E84"),sQuery(id+"F0.wireOp",EDGE,"E85"),sQuery(id+"F0.wireOp",EDGE,"E86"),sQuery(id+"F0.wireOp",EDGE,"E87"),sQuery(id+"F0.wireOp",EDGE,"E88"),sQuery(id+"F0.wireOp",EDGE,"E89"),sQuery(id+"F0.wireOp",EDGE,"E90"),sQuery(id+"F0.wireOp",EDGE,"E91"),sQuery(id+"F0.wireOp",EDGE,"E92"),sQuery(id+"F0.wireOp",EDGE,"E93"),sQuery(id+"F0.wireOp",EDGE,"E94"),sQuery(id+"F0.wireOp",EDGE,"E95"),sQuery(id+"F0.wireOp",EDGE,"E96"),sQuery(id+"F0.wireOp",EDGE,"E97"),sQuery(id+"F0.wireOp",EDGE,"E98"),sQuery(id+"F0.wireOp",EDGE,"E99"),sQuery(id+"F0.wireOp",EDGE,"E100"),sQuery(id+"F0.wireOp",EDGE,"E101"),sQuery(id+"F0.wireOp",EDGE,"E102"),sQuery(id+"F0.wireOp",EDGE,"E103"),sQuery(id+"F0.wireOp",EDGE,"E104"),sQuery(id+"F0.wireOp",EDGE,"E105"),sQuery(id+"F0.wireOp",EDGE,"E106"),sQuery(id+"F0.wireOp",EDGE,"E107"),sQuery(id+"F0.wireOp",EDGE,"E108"),sQuery(id+"F0.wireOp",EDGE,"E109"),sQuery(id+"F0.wireOp",EDGE,"E110"),sQuery(id+"F0.wireOp",EDGE,"E111"),sQuery(id+"F0.wireOp",EDGE,"E112"),sQuery(id+"F0.wireOp",EDGE,"E113"),sQuery(id+"F0.wireOp",EDGE,"E114"),sQuery(id+"F0.wireOp",EDGE,"E115"),sQuery(id+"F0.wireOp",EDGE,"E116"),sQuery(id+"F0.wireOp",EDGE,"E117"),sQuery(id+"F0.wireOp",EDGE,"E118"),sQuery(id+"F0.wireOp",EDGE,"E119"),sQuery(id+"F0.wireOp",EDGE,"E120"),sQuery(id+"F0.wireOp",EDGE,"E121"),sQuery(id+"F0.wireOp",EDGE,"E122"),sQuery(id+"F0.wireOp",EDGE,"E123"),sQuery(id+"F0.wireOp",EDGE,"E124"),sQuery(id+"F0.wireOp",EDGE,"E125"),sQuery(id+"F0.wireOp",EDGE,"E126"),sQuery(id+"F0.wireOp",EDGE,"E127"),sQuery(id+"F0.wireOp",EDGE,"E128"),sQuery(id+"F0.wireOp",EDGE,"E129"),sQuery(id+"F0.wireOp",EDGE,"E130"),sQuery(id+"F0.wireOp",EDGE,"E131"),sQuery(id+"F0.wireOp",EDGE,"E132"),sQuery(id+"F0.wireOp",EDGE,"E133"),sQuery(id+"F0.wireOp",EDGE,"E134"),sQuery(id+"F0.wireOp",EDGE,"E135"),sQuery(id+"F0.wireOp",EDGE,"E136"),sQuery(id+"F0.wireOp",EDGE,"E137"),sQuery(id+"F0.wireOp",EDGE,"E138"),sQuery(id+"F0.wireOp",EDGE,"E139"),sQuery(id+"F0.wireOp",EDGE,"E140"),sQuery(id+"F0.wireOp",EDGE,"E141"),sQuery(id+"F0.wireOp",EDGE,"E142"),sQuery(id+"F0.wireOp",EDGE,"E143"),sQuery(id+"F0.wireOp",EDGE,"E144"),sQuery(id+"F0.wireOp",EDGE,"E145"),sQuery(id+"F0.wireOp",EDGE,"E146"),sQuery(id+"F0.wireOp",EDGE,"E147"),sQuery(id+"F0.wireOp",EDGE,"E148"),sQuery(id+"F0.wireOp",EDGE,"E149"),sQuery(id+"F0.wireOp",EDGE,"E150"),sQuery(id+"F0.wireOp",EDGE,"E151"),sQuery(id+"F0.wireOp",EDGE,"E152"),sQuery(id+"F0.wireOp",EDGE,"E153"),sQuery(id+"F0.wireOp",EDGE,"E154"),sQuery(id+"F0.wireOp",EDGE,"E155"),sQuery(id+"F0.wireOp",EDGE,"E156"),sQuery(id+"F0.wireOp",EDGE,"E157"),sQuery(id+"F0.wireOp",EDGE,"E158"),sQuery(id+"F0.wireOp",EDGE,"E159"),sQuery(id+"F0.wireOp",EDGE,"E160"),sQuery(id+"F0.wireOp",EDGE,"E161"),sQuery(id+"F0.wireOp",EDGE,"E162"),sQuery(id+"F0.wireOp",EDGE,"E163")])],"isStart":false});
            var sketch = newSketch(context, id + "F27", { "sketchPlane" : qUnion([Q0])});
            skCircle(sketch, "E188", {"center": v(39.27, 45.04) * mm, "radius": 0.62 * mm});
            skSolve(sketch);
        }
        {
            var Q0;
            Q0 = qSketchRegion(id + "F27", true);
            extrude(context, id + "F28", {"entities" : qUnion([Q0]), "operationType" : NewBodyOperationType.REMOVE, "oppositeDirection" : true, "depth" : 3.8 * mm, "offsetDistance" : 25 * mm});
        }
        {
            var Q0;
            Q0=makeQuery(id+"F1.opExtrude","CAP_FACE",FACE,{"disambiguationData":[OSD([sQuery(id+"F0.wireOp",EDGE,"E0"),sQuery(id+"F0.wireOp",EDGE,"E1"),sQuery(id+"F0.wireOp",EDGE,"E2"),sQuery(id+"F0.wireOp",EDGE,"E3"),sQuery(id+"F0.wireOp",EDGE,"E4"),sQuery(id+"F0.wireOp",EDGE,"E5"),sQuery(id+"F0.wireOp",EDGE,"E6"),sQuery(id+"F0.wireOp",EDGE,"E7"),sQuery(id+"F0.wireOp",EDGE,"E8"),sQuery(id+"F0.wireOp",EDGE,"E9"),sQuery(id+"F0.wireOp",EDGE,"E10"),sQuery(id+"F0.wireOp",EDGE,"E11"),sQuery(id+"F0.wireOp",EDGE,"E12"),sQuery(id+"F0.wireOp",EDGE,"E13"),sQuery(id+"F0.wireOp",EDGE,"E14"),sQuery(id+"F0.wireOp",EDGE,"E15"),sQuery(id+"F0.wireOp",EDGE,"E16"),sQuery(id+"F0.wireOp",EDGE,"E17"),sQuery(id+"F0.wireOp",EDGE,"E18"),sQuery(id+"F0.wireOp",EDGE,"E19"),sQuery(id+"F0.wireOp",EDGE,"E20"),sQuery(id+"F0.wireOp",EDGE,"E21"),sQuery(id+"F0.wireOp",EDGE,"E22"),sQuery(id+"F0.wireOp",EDGE,"E23"),sQuery(id+"F0.wireOp",EDGE,"E24"),sQuery(id+"F0.wireOp",EDGE,"E25"),sQuery(id+"F0.wireOp",EDGE,"E26"),sQuery(id+"F0.wireOp",EDGE,"E27"),sQuery(id+"F0.wireOp",EDGE,"E28"),sQuery(id+"F0.wireOp",EDGE,"E29"),sQuery(id+"F0.wireOp",EDGE,"E30"),sQuery(id+"F0.wireOp",EDGE,"E31"),sQuery(id+"F0.wireOp",EDGE,"E32"),sQuery(id+"F0.wireOp",EDGE,"E33"),sQuery(id+"F0.wireOp",EDGE,"E34"),sQuery(id+"F0.wireOp",EDGE,"E35"),sQuery(id+"F0.wireOp",EDGE,"E36"),sQuery(id+"F0.wireOp",EDGE,"E37"),sQuery(id+"F0.wireOp",EDGE,"E38"),sQuery(id+"F0.wireOp",EDGE,"E39"),sQuery(id+"F0.wireOp",EDGE,"E40"),sQuery(id+"F0.wireOp",EDGE,"E41"),sQuery(id+"F0.wireOp",EDGE,"E42"),sQuery(id+"F0.wireOp",EDGE,"E43"),sQuery(id+"F0.wireOp",EDGE,"E44"),sQuery(id+"F0.wireOp",EDGE,"E45"),sQuery(id+"F0.wireOp",EDGE,"E46"),sQuery(id+"F0.wireOp",EDGE,"E47"),sQuery(id+"F0.wireOp",EDGE,"E48"),sQuery(id+"F0.wireOp",EDGE,"E49"),sQuery(id+"F0.wireOp",EDGE,"E50"),sQuery(id+"F0.wireOp",EDGE,"E51"),sQuery(id+"F0.wireOp",EDGE,"E52"),sQuery(id+"F0.wireOp",EDGE,"E53"),sQuery(id+"F0.wireOp",EDGE,"E54"),sQuery(id+"F0.wireOp",EDGE,"E55"),sQuery(id+"F0.wireOp",EDGE,"E56"),sQuery(id+"F0.wireOp",EDGE,"E57"),sQuery(id+"F0.wireOp",EDGE,"E58"),sQuery(id+"F0.wireOp",EDGE,"E59"),sQuery(id+"F0.wireOp",EDGE,"E60"),sQuery(id+"F0.wireOp",EDGE,"E61"),sQuery(id+"F0.wireOp",EDGE,"E62"),sQuery(id+"F0.wireOp",EDGE,"E63"),sQuery(id+"F0.wireOp",EDGE,"E64"),sQuery(id+"F0.wireOp",EDGE,"E65"),sQuery(id+"F0.wireOp",EDGE,"E66"),sQuery(id+"F0.wireOp",EDGE,"E67"),sQuery(id+"F0.wireOp",EDGE,"E68"),sQuery(id+"F0.wireOp",EDGE,"E69"),sQuery(id+"F0.wireOp",EDGE,"E70"),sQuery(id+"F0.wireOp",EDGE,"E71"),sQuery(id+"F0.wireOp",EDGE,"E72"),sQuery(id+"F0.wireOp",EDGE,"E73"),sQuery(id+"F0.wireOp",EDGE,"E74"),sQuery(id+"F0.wireOp",EDGE,"E75"),sQuery(id+"F0.wireOp",EDGE,"E76"),sQuery(id+"F0.wireOp",EDGE,"E77"),sQuery(id+"F0.wireOp",EDGE,"E78"),sQuery(id+"F0.wireOp",EDGE,"E79"),sQuery(id+"F0.wireOp",EDGE,"E80"),sQuery(id+"F0.wireOp",EDGE,"E81"),sQuery(id+"F0.wireOp",EDGE,"E82"),sQuery(id+"F0.wireOp",EDGE,"E83"),sQuery(id+"F0.wireOp",EDGE,"E84"),sQuery(id+"F0.wireOp",EDGE,"E85"),sQuery(id+"F0.wireOp",EDGE,"E86"),sQuery(id+"F0.wireOp",EDGE,"E87"),sQuery(id+"F0.wireOp",EDGE,"E88"),sQuery(id+"F0.wireOp",EDGE,"E89"),sQuery(id+"F0.wireOp",EDGE,"E90"),sQuery(id+"F0.wireOp",EDGE,"E91"),sQuery(id+"F0.wireOp",EDGE,"E92"),sQuery(id+"F0.wireOp",EDGE,"E93"),sQuery(id+"F0.wireOp",EDGE,"E94"),sQuery(id+"F0.wireOp",EDGE,"E95"),sQuery(id+"F0.wireOp",EDGE,"E96"),sQuery(id+"F0.wireOp",EDGE,"E97"),sQuery(id+"F0.wireOp",EDGE,"E98"),sQuery(id+"F0.wireOp",EDGE,"E99"),sQuery(id+"F0.wireOp",EDGE,"E100"),sQuery(id+"F0.wireOp",EDGE,"E101"),sQuery(id+"F0.wireOp",EDGE,"E102"),sQuery(id+"F0.wireOp",EDGE,"E103"),sQuery(id+"F0.wireOp",EDGE,"E104"),sQuery(id+"F0.wireOp",EDGE,"E105"),sQuery(id+"F0.wireOp",EDGE,"E106"),sQuery(id+"F0.wireOp",EDGE,"E107"),sQuery(id+"F0.wireOp",EDGE,"E108"),sQuery(id+"F0.wireOp",EDGE,"E109"),sQuery(id+"F0.wireOp",EDGE,"E110"),sQuery(id+"F0.wireOp",EDGE,"E111"),sQuery(id+"F0.wireOp",EDGE,"E112"),sQuery(id+"F0.wireOp",EDGE,"E113"),sQuery(id+"F0.wireOp",EDGE,"E114"),sQuery(id+"F0.wireOp",EDGE,"E115"),sQuery(id+"F0.wireOp",EDGE,"E116"),sQuery(id+"F0.wireOp",EDGE,"E117"),sQuery(id+"F0.wireOp",EDGE,"E118"),sQuery(id+"F0.wireOp",EDGE,"E119"),sQuery(id+"F0.wireOp",EDGE,"E120"),sQuery(id+"F0.wireOp",EDGE,"E121"),sQuery(id+"F0.wireOp",EDGE,"E122"),sQuery(id+"F0.wireOp",EDGE,"E123"),sQuery(id+"F0.wireOp",EDGE,"E124"),sQuery(id+"F0.wireOp",EDGE,"E125"),sQuery(id+"F0.wireOp",EDGE,"E126"),sQuery(id+"F0.wireOp",EDGE,"E127"),sQuery(id+"F0.wireOp",EDGE,"E128"),sQuery(id+"F0.wireOp",EDGE,"E129"),sQuery(id+"F0.wireOp",EDGE,"E130"),sQuery(id+"F0.wireOp",EDGE,"E131"),sQuery(id+"F0.wireOp",EDGE,"E132"),sQuery(id+"F0.wireOp",EDGE,"E133"),sQuery(id+"F0.wireOp",EDGE,"E134"),sQuery(id+"F0.wireOp",EDGE,"E135"),sQuery(id+"F0.wireOp",EDGE,"E136"),sQuery(id+"F0.wireOp",EDGE,"E137"),sQuery(id+"F0.wireOp",EDGE,"E138"),sQuery(id+"F0.wireOp",EDGE,"E139"),sQuery(id+"F0.wireOp",EDGE,"E140"),sQuery(id+"F0.wireOp",EDGE,"E141"),sQuery(id+"F0.wireOp",EDGE,"E142"),sQuery(id+"F0.wireOp",EDGE,"E143"),sQuery(id+"F0.wireOp",EDGE,"E144"),sQuery(id+"F0.wireOp",EDGE,"E145"),sQuery(id+"F0.wireOp",EDGE,"E146"),sQuery(id+"F0.wireOp",EDGE,"E147"),sQuery(id+"F0.wireOp",EDGE,"E148"),sQuery(id+"F0.wireOp",EDGE,"E149"),sQuery(id+"F0.wireOp",EDGE,"E150"),sQuery(id+"F0.wireOp",EDGE,"E151"),sQuery(id+"F0.wireOp",EDGE,"E152"),sQuery(id+"F0.wireOp",EDGE,"E153"),sQuery(id+"F0.wireOp",EDGE,"E154"),sQuery(id+"F0.wireOp",EDGE,"E155"),sQuery(id+"F0.wireOp",EDGE,"E156"),sQuery(id+"F0.wireOp",EDGE,"E157"),sQuery(id+"F0.wireOp",EDGE,"E158"),sQuery(id+"F0.wireOp",EDGE,"E159"),sQuery(id+"F0.wireOp",EDGE,"E160"),sQuery(id+"F0.wireOp",EDGE,"E161"),sQuery(id+"F0.wireOp",EDGE,"E162"),sQuery(id+"F0.wireOp",EDGE,"E163")])],"isStart":true});
            var sketch = newSketch(context, id + "F29", { "sketchPlane" : qUnion([Q0])});
            skCircle(sketch, "E189", {"center": v(-35.56, 53.96) * mm, "radius": 0.68 * mm});
            skSolve(sketch);
        }
        {
            var Q0;
            Q0 = qSketchRegion(id + "F29", true);
            extrude(context, id + "F30", {"entities" : qUnion([Q0]), "operationType" : NewBodyOperationType.ADD, "depth" : 2.9 * mm, "offsetDistance" : 25 * mm});
        }
        {
            var Q0;
            Q0=makeQuery(id+"F1.opExtrude","CAP_FACE",FACE,{"disambiguationData":[OSD([sQuery(id+"F0.wireOp",EDGE,"E0"),sQuery(id+"F0.wireOp",EDGE,"E1"),sQuery(id+"F0.wireOp",EDGE,"E2"),sQuery(id+"F0.wireOp",EDGE,"E3"),sQuery(id+"F0.wireOp",EDGE,"E4"),sQuery(id+"F0.wireOp",EDGE,"E5"),sQuery(id+"F0.wireOp",EDGE,"E6"),sQuery(id+"F0.wireOp",EDGE,"E7"),sQuery(id+"F0.wireOp",EDGE,"E8"),sQuery(id+"F0.wireOp",EDGE,"E9"),sQuery(id+"F0.wireOp",EDGE,"E10"),sQuery(id+"F0.wireOp",EDGE,"E11"),sQuery(id+"F0.wireOp",EDGE,"E12"),sQuery(id+"F0.wireOp",EDGE,"E13"),sQuery(id+"F0.wireOp",EDGE,"E14"),sQuery(id+"F0.wireOp",EDGE,"E15"),sQuery(id+"F0.wireOp",EDGE,"E16"),sQuery(id+"F0.wireOp",EDGE,"E17"),sQuery(id+"F0.wireOp",EDGE,"E18"),sQuery(id+"F0.wireOp",EDGE,"E19"),sQuery(id+"F0.wireOp",EDGE,"E20"),sQuery(id+"F0.wireOp",EDGE,"E21"),sQuery(id+"F0.wireOp",EDGE,"E22"),sQuery(id+"F0.wireOp",EDGE,"E23"),sQuery(id+"F0.wireOp",EDGE,"E24"),sQuery(id+"F0.wireOp",EDGE,"E25"),sQuery(id+"F0.wireOp",EDGE,"E26"),sQuery(id+"F0.wireOp",EDGE,"E27"),sQuery(id+"F0.wireOp",EDGE,"E28"),sQuery(id+"F0.wireOp",EDGE,"E29"),sQuery(id+"F0.wireOp",EDGE,"E30"),sQuery(id+"F0.wireOp",EDGE,"E31"),sQuery(id+"F0.wireOp",EDGE,"E32"),sQuery(id+"F0.wireOp",EDGE,"E33"),sQuery(id+"F0.wireOp",EDGE,"E34"),sQuery(id+"F0.wireOp",EDGE,"E35"),sQuery(id+"F0.wireOp",EDGE,"E36"),sQuery(id+"F0.wireOp",EDGE,"E37"),sQuery(id+"F0.wireOp",EDGE,"E38"),sQuery(id+"F0.wireOp",EDGE,"E39"),sQuery(id+"F0.wireOp",EDGE,"E40"),sQuery(id+"F0.wireOp",EDGE,"E41"),sQuery(id+"F0.wireOp",EDGE,"E42"),sQuery(id+"F0.wireOp",EDGE,"E43"),sQuery(id+"F0.wireOp",EDGE,"E44"),sQuery(id+"F0.wireOp",EDGE,"E45"),sQuery(id+"F0.wireOp",EDGE,"E46"),sQuery(id+"F0.wireOp",EDGE,"E47"),sQuery(id+"F0.wireOp",EDGE,"E48"),sQuery(id+"F0.wireOp",EDGE,"E49"),sQuery(id+"F0.wireOp",EDGE,"E50"),sQuery(id+"F0.wireOp",EDGE,"E51"),sQuery(id+"F0.wireOp",EDGE,"E52"),sQuery(id+"F0.wireOp",EDGE,"E53"),sQuery(id+"F0.wireOp",EDGE,"E54"),sQuery(id+"F0.wireOp",EDGE,"E55"),sQuery(id+"F0.wireOp",EDGE,"E56"),sQuery(id+"F0.wireOp",EDGE,"E57"),sQuery(id+"F0.wireOp",EDGE,"E58"),sQuery(id+"F0.wireOp",EDGE,"E59"),sQuery(id+"F0.wireOp",EDGE,"E60"),sQuery(id+"F0.wireOp",EDGE,"E61"),sQuery(id+"F0.wireOp",EDGE,"E62"),sQuery(id+"F0.wireOp",EDGE,"E63"),sQuery(id+"F0.wireOp",EDGE,"E64"),sQuery(id+"F0.wireOp",EDGE,"E65"),sQuery(id+"F0.wireOp",EDGE,"E66"),sQuery(id+"F0.wireOp",EDGE,"E67"),sQuery(id+"F0.wireOp",EDGE,"E68"),sQuery(id+"F0.wireOp",EDGE,"E69"),sQuery(id+"F0.wireOp",EDGE,"E70"),sQuery(id+"F0.wireOp",EDGE,"E71"),sQuery(id+"F0.wireOp",EDGE,"E72"),sQuery(id+"F0.wireOp",EDGE,"E73"),sQuery(id+"F0.wireOp",EDGE,"E74"),sQuery(id+"F0.wireOp",EDGE,"E75"),sQuery(id+"F0.wireOp",EDGE,"E76"),sQuery(id+"F0.wireOp",EDGE,"E77"),sQuery(id+"F0.wireOp",EDGE,"E78"),sQuery(id+"F0.wireOp",EDGE,"E79"),sQuery(id+"F0.wireOp",EDGE,"E80"),sQuery(id+"F0.wireOp",EDGE,"E81"),sQuery(id+"F0.wireOp",EDGE,"E82"),sQuery(id+"F0.wireOp",EDGE,"E83"),sQuery(id+"F0.wireOp",EDGE,"E84"),sQuery(id+"F0.wireOp",EDGE,"E85"),sQuery(id+"F0.wireOp",EDGE,"E86"),sQuery(id+"F0.wireOp",EDGE,"E87"),sQuery(id+"F0.wireOp",EDGE,"E88"),sQuery(id+"F0.wireOp",EDGE,"E89"),sQuery(id+"F0.wireOp",EDGE,"E90"),sQuery(id+"F0.wireOp",EDGE,"E91"),sQuery(id+"F0.wireOp",EDGE,"E92"),sQuery(id+"F0.wireOp",EDGE,"E93"),sQuery(id+"F0.wireOp",EDGE,"E94"),sQuery(id+"F0.wireOp",EDGE,"E95"),sQuery(id+"F0.wireOp",EDGE,"E96"),sQuery(id+"F0.wireOp",EDGE,"E97"),sQuery(id+"F0.wireOp",EDGE,"E98"),sQuery(id+"F0.wireOp",EDGE,"E99"),sQuery(id+"F0.wireOp",EDGE,"E100"),sQuery(id+"F0.wireOp",EDGE,"E101"),sQuery(id+"F0.wireOp",EDGE,"E102"),sQuery(id+"F0.wireOp",EDGE,"E103"),sQuery(id+"F0.wireOp",EDGE,"E104"),sQuery(id+"F0.wireOp",EDGE,"E105"),sQuery(id+"F0.wireOp",EDGE,"E106"),sQuery(id+"F0.wireOp",EDGE,"E107"),sQuery(id+"F0.wireOp",EDGE,"E108"),sQuery(id+"F0.wireOp",EDGE,"E109"),sQuery(id+"F0.wireOp",EDGE,"E110"),sQuery(id+"F0.wireOp",EDGE,"E111"),sQuery(id+"F0.wireOp",EDGE,"E112"),sQuery(id+"F0.wireOp",EDGE,"E113"),sQuery(id+"F0.wireOp",EDGE,"E114"),sQuery(id+"F0.wireOp",EDGE,"E115"),sQuery(id+"F0.wireOp",EDGE,"E116"),sQuery(id+"F0.wireOp",EDGE,"E117"),sQuery(id+"F0.wireOp",EDGE,"E118"),sQuery(id+"F0.wireOp",EDGE,"E119"),sQuery(id+"F0.wireOp",EDGE,"E120"),sQuery(id+"F0.wireOp",EDGE,"E121"),sQuery(id+"F0.wireOp",EDGE,"E122"),sQuery(id+"F0.wireOp",EDGE,"E123"),sQuery(id+"F0.wireOp",EDGE,"E124"),sQuery(id+"F0.wireOp",EDGE,"E125"),sQuery(id+"F0.wireOp",EDGE,"E126"),sQuery(id+"F0.wireOp",EDGE,"E127"),sQuery(id+"F0.wireOp",EDGE,"E128"),sQuery(id+"F0.wireOp",EDGE,"E129"),sQuery(id+"F0.wireOp",EDGE,"E130"),sQuery(id+"F0.wireOp",EDGE,"E131"),sQuery(id+"F0.wireOp",EDGE,"E132"),sQuery(id+"F0.wireOp",EDGE,"E133"),sQuery(id+"F0.wireOp",EDGE,"E134"),sQuery(id+"F0.wireOp",EDGE,"E135"),sQuery(id+"F0.wireOp",EDGE,"E136"),sQuery(id+"F0.wireOp",EDGE,"E137"),sQuery(id+"F0.wireOp",EDGE,"E138"),sQuery(id+"F0.wireOp",EDGE,"E139"),sQuery(id+"F0.wireOp",EDGE,"E140"),sQuery(id+"F0.wireOp",EDGE,"E141"),sQuery(id+"F0.wireOp",EDGE,"E142"),sQuery(id+"F0.wireOp",EDGE,"E143"),sQuery(id+"F0.wireOp",EDGE,"E144"),sQuery(id+"F0.wireOp",EDGE,"E145"),sQuery(id+"F0.wireOp",EDGE,"E146"),sQuery(id+"F0.wireOp",EDGE,"E147"),sQuery(id+"F0.wireOp",EDGE,"E148"),sQuery(id+"F0.wireOp",EDGE,"E149"),sQuery(id+"F0.wireOp",EDGE,"E150"),sQuery(id+"F0.wireOp",EDGE,"E151"),sQuery(id+"F0.wireOp",EDGE,"E152"),sQuery(id+"F0.wireOp",EDGE,"E153"),sQuery(id+"F0.wireOp",EDGE,"E154"),sQuery(id+"F0.wireOp",EDGE,"E155"),sQuery(id+"F0.wireOp",EDGE,"E156"),sQuery(id+"F0.wireOp",EDGE,"E157"),sQuery(id+"F0.wireOp",EDGE,"E158"),sQuery(id+"F0.wireOp",EDGE,"E159"),sQuery(id+"F0.wireOp",EDGE,"E160"),sQuery(id+"F0.wireOp",EDGE,"E161"),sQuery(id+"F0.wireOp",EDGE,"E162"),sQuery(id+"F0.wireOp",EDGE,"E163")])],"isStart":true});
            var sketch = newSketch(context, id + "F31", { "sketchPlane" : qUnion([Q0])});
            skCircle(sketch, "E190", {"center": v(-41.98, 55.8) * mm, "radius": 0.6 * mm});
            skSolve(sketch);
        }
        {
            var Q0;
            Q0 = qSketchRegion(id + "F31", true);
            extrude(context, id + "F32", {"entities" : qUnion([Q0]), "operationType" : NewBodyOperationType.ADD, "depth" : 3.13 * mm, "offsetDistance" : 25 * mm});
        }
    });
